FCSTD DOCUMENT  (FreeCAD 0.18R16110 (Git))
Label: plate
License: All rights reserved
LicenseURL: http://en.wikipedia.org/wiki/All_rights_reserved
objects: Part::Part2DObjectPython×463, App::DocumentObjectGroup×68
note: 463 computed .brp shape members not serialized (recipe doc carries the construction recipe); baked Part::Feature solids carry a one-line shape summary decoded from their .brp

FEATURE [Part::Part2DObjectPython] Arc  # Draft 2D object (typed FeaturePython)
  FirstAngle = 90
  LastAngle = 180
  MakeFace = true
  Placement = pos=(2.8,-2.8,0) rot=(0,0,1;0rad)
  Radius = 0.3
FEATURE [Part::Part2DObjectPython] Arc001  # Draft 2D object (typed FeaturePython)
  FirstAngle = 90
  LastAngle = 180
  MakeFace = true
  Placement = pos=(16.2,-2.8,0) rot=(0,0,-1;1.5708rad)
  Radius = 0.3
FEATURE [Part::Part2DObjectPython] Arc002  # Draft 2D object (typed FeaturePython)
  FirstAngle = 90
  LastAngle = 180
  MakeFace = true
  Placement = pos=(16.2,-16.2,0) rot=(0,0,1;3.14159rad)
  Radius = 0.3
FEATURE [Part::Part2DObjectPython] Arc003  # Draft 2D object (typed FeaturePython)
  FirstAngle = 90
  LastAngle = 180
  MakeFace = true
  Placement = pos=(2.8,-16.2,0) rot=(0,0,1;1.5708rad)
  Radius = 0.3
FEATURE [Part::Part2DObjectPython] Line012  # Draft 2D object (typed FeaturePython)
  ChamferSize = 0
  Closed = false
  End = (16.2,-2.5,0)
  FilletRadius = 0
  Length = 13.4
  MakeFace = true
  Points = (2) [(2.8,-2.5,0),(16.2,-2.5,0)]
  Start = (2.8,-2.5,0)
  Subdivisions = 0
FEATURE [Part::Part2DObjectPython] Line013  # Draft 2D object (typed FeaturePython)
  ChamferSize = 0
  Closed = false
  End = (16.5,-16.2,0)
  FilletRadius = 0
  Length = 13.4
  MakeFace = true
  Points = (2) [(16.5,-2.8,0),(16.5,-16.2,0)]
  Start = (16.5,-2.8,0)
  Subdivisions = 0
FEATURE [Part::Part2DObjectPython] Line014  # Draft 2D object (typed FeaturePython)
  ChamferSize = 0
  Closed = false
  End = (2.8,-16.5,0)
  FilletRadius = 0
  Length = 13.4
  MakeFace = true
  Points = (2) [(16.2,-16.5,0),(2.8,-16.5,0)]
  Start = (16.2,-16.5,0)
  Subdivisions = 0
FEATURE [Part::Part2DObjectPython] Line015  # Draft 2D object (typed FeaturePython)
  ChamferSize = 0
  Closed = false
  End = (2.5,-2.8,0)
  FilletRadius = 0
  Length = 13.4
  MakeFace = true
  Points = (2) [(2.5,-16.2,0),(2.5,-2.8,0)]
  Start = (2.5,-16.2,0)
  Subdivisions = 0
FEATURE [App::DocumentObjectGroup] Group
  Group = -> [Arc,Arc001,Arc002,Arc003,Line012,Line013,Line014,Line015]
FEATURE [Part::Part2DObjectPython] Arc004  # Draft 2D object (typed FeaturePython)
  FirstAngle = 90
  LastAngle = 180
  MakeFace = true
  Placement = pos=(21.8,-2.8,0) rot=(0,0,1;0rad)
  Radius = 0.3
FEATURE [Part::Part2DObjectPython] Line020  # Draft 2D object (typed FeaturePython)
  ChamferSize = 0
  Closed = false
  End = (21.8,-16.5,0)
  FilletRadius = 0
  Length = 13.4
  MakeFace = true
  Placement = pos=(19,0,0) rot=(0,0,1;0rad)
  Points = (2) [(16.2,-16.5,0),(2.8,-16.5,0)]
  Start = (35.2,-16.5,0)
  Subdivisions = 0
FEATURE [Part::Part2DObjectPython] Arc005  # Draft 2D object (typed FeaturePython)
  FirstAngle = 90
  LastAngle = 180
  MakeFace = true
  Placement = pos=(35.2,-16.2,0) rot=(0,0,1;3.14159rad)
  Radius = 0.3
FEATURE [Part::Part2DObjectPython] Line022  # Draft 2D object (typed FeaturePython)
  ChamferSize = 0
  Closed = false
  End = (21.5,-2.8,0)
  FilletRadius = 0
  Length = 13.4
  MakeFace = true
  Placement = pos=(19,0,0) rot=(0,0,1;0rad)
  Points = (2) [(2.5,-16.2,0),(2.5,-2.8,0)]
  Start = (21.5,-16.2,0)
  Subdivisions = 0
FEATURE [Part::Part2DObjectPython] Arc006  # Draft 2D object (typed FeaturePython)
  FirstAngle = 90
  LastAngle = 180
  MakeFace = true
  Placement = pos=(21.8,-16.2,0) rot=(0,0,1;1.5708rad)
  Radius = 0.3
FEATURE [Part::Part2DObjectPython] Line023  # Draft 2D object (typed FeaturePython)
  ChamferSize = 0
  Closed = false
  End = (35.2,-2.5,0)
  FilletRadius = 0
  Length = 13.4
  MakeFace = true
  Placement = pos=(19,0,0) rot=(0,0,1;0rad)
  Points = (2) [(2.8,-2.5,0),(16.2,-2.5,0)]
  Start = (21.8,-2.5,0)
  Subdivisions = 0
FEATURE [Part::Part2DObjectPython] Arc007  # Draft 2D object (typed FeaturePython)
  FirstAngle = 90
  LastAngle = 180
  MakeFace = true
  Placement = pos=(35.2,-2.8,0) rot=(0,0,-1;1.5708rad)
  Radius = 0.3
FEATURE [App::DocumentObjectGroup] Group001
  Group = -> [Arc004,Arc007,Arc005,Arc006,Line023,Line020,Line022]
FEATURE [Part::Part2DObjectPython] Arc008  # Draft 2D object (typed FeaturePython)
  FirstAngle = 90
  LastAngle = 180
  MakeFace = true
  Placement = pos=(40.8,-2.8,0) rot=(0,0,1;0rad)
  Radius = 0.3
FEATURE [Part::Part2DObjectPython] Line030  # Draft 2D object (typed FeaturePython)
  ChamferSize = 0
  Closed = false
  End = (40.8,-16.5,0)
  FilletRadius = 0
  Length = 13.4
  MakeFace = true
  Placement = pos=(38,0,0) rot=(0,0,1;0rad)
  Points = (2) [(16.2,-16.5,0),(2.8,-16.5,0)]
  Start = (54.2,-16.5,0)
  Subdivisions = 0
FEATURE [Part::Part2DObjectPython] Line031  # Draft 2D object (typed FeaturePython)
  ChamferSize = 0
  Closed = false
  End = (54.5,-16.2,0)
  FilletRadius = 0
  Length = 13.4
  MakeFace = true
  Placement = pos=(38,0,0) rot=(0,0,1;0rad)
  Points = (2) [(16.5,-2.8,0),(16.5,-16.2,0)]
  Start = (54.5,-2.8,0)
  Subdivisions = 0
FEATURE [Part::Part2DObjectPython] Arc009  # Draft 2D object (typed FeaturePython)
  FirstAngle = 90
  LastAngle = 180
  MakeFace = true
  Placement = pos=(54.2,-16.2,0) rot=(0,0,1;3.14159rad)
  Radius = 0.3
FEATURE [Part::Part2DObjectPython] Arc010  # Draft 2D object (typed FeaturePython)
  FirstAngle = 90
  LastAngle = 180
  MakeFace = true
  Placement = pos=(40.8,-16.2,0) rot=(0,0,1;1.5708rad)
  Radius = 0.3
FEATURE [Part::Part2DObjectPython] Line033  # Draft 2D object (typed FeaturePython)
  ChamferSize = 0
  Closed = false
  End = (54.2,-2.5,0)
  FilletRadius = 0
  Length = 13.4
  MakeFace = true
  Placement = pos=(38,0,0) rot=(0,0,1;0rad)
  Points = (2) [(2.8,-2.5,0),(16.2,-2.5,0)]
  Start = (40.8,-2.5,0)
  Subdivisions = 0
FEATURE [Part::Part2DObjectPython] Arc011  # Draft 2D object (typed FeaturePython)
  FirstAngle = 90
  LastAngle = 180
  MakeFace = true
  Placement = pos=(54.2,-2.8,0) rot=(0,0,-1;1.5708rad)
  Radius = 0.3
FEATURE [App::DocumentObjectGroup] Group002
  Group = -> [Arc008,Arc011,Arc009,Arc010,Line033,Line031,Line030]
FEATURE [Part::Part2DObjectPython] Arc012  # Draft 2D object (typed FeaturePython)
  FirstAngle = 90
  LastAngle = 180
  MakeFace = true
  Placement = pos=(59.8,-2.8,0) rot=(0,0,1;0rad)
  Radius = 0.3
FEATURE [Part::Part2DObjectPython] Line040  # Draft 2D object (typed FeaturePython)
  ChamferSize = 0
  Closed = false
  End = (59.8,-16.5,0)
  FilletRadius = 0
  Length = 13.4
  MakeFace = true
  Placement = pos=(57,0,0) rot=(0,0,1;0rad)
  Points = (2) [(16.2,-16.5,0),(2.8,-16.5,0)]
  Start = (73.2,-16.5,0)
  Subdivisions = 0
FEATURE [Part::Part2DObjectPython] Line041  # Draft 2D object (typed FeaturePython)
  ChamferSize = 0
  Closed = false
  End = (73.5,-16.2,0)
  FilletRadius = 0
  Length = 13.4
  MakeFace = true
  Placement = pos=(57,0,0) rot=(0,0,1;0rad)
  Points = (2) [(16.5,-2.8,0),(16.5,-16.2,0)]
  Start = (73.5,-2.8,0)
  Subdivisions = 0
FEATURE [Part::Part2DObjectPython] Arc013  # Draft 2D object (typed FeaturePython)
  FirstAngle = 90
  LastAngle = 180
  MakeFace = true
  Placement = pos=(73.2,-16.2,0) rot=(0,0,1;3.14159rad)
  Radius = 0.3
FEATURE [Part::Part2DObjectPython] Line042  # Draft 2D object (typed FeaturePython)
  ChamferSize = 0
  Closed = false
  End = (59.5,-2.8,0)
  FilletRadius = 0
  Length = 13.4
  MakeFace = true
  Placement = pos=(57,0,0) rot=(0,0,1;0rad)
  Points = (2) [(2.5,-16.2,0),(2.5,-2.8,0)]
  Start = (59.5,-16.2,0)
  Subdivisions = 0
FEATURE [Part::Part2DObjectPython] Arc014  # Draft 2D object (typed FeaturePython)
  FirstAngle = 90
  LastAngle = 180
  MakeFace = true
  Placement = pos=(59.8,-16.2,0) rot=(0,0,1;1.5708rad)
  Radius = 0.3
FEATURE [Part::Part2DObjectPython] Line043  # Draft 2D object (typed FeaturePython)
  ChamferSize = 0
  Closed = false
  End = (73.2,-2.5,0)
  FilletRadius = 0
  Length = 13.4
  MakeFace = true
  Placement = pos=(57,0,0) rot=(0,0,1;0rad)
  Points = (2) [(2.8,-2.5,0),(16.2,-2.5,0)]
  Start = (59.8,-2.5,0)
  Subdivisions = 0
FEATURE [Part::Part2DObjectPython] Arc015  # Draft 2D object (typed FeaturePython)
  FirstAngle = 90
  LastAngle = 180
  MakeFace = true
  Placement = pos=(73.2,-2.8,0) rot=(0,0,-1;1.5708rad)
  Radius = 0.3
FEATURE [App::DocumentObjectGroup] Group003
  Group = -> [Arc012,Arc015,Arc013,Arc014,Line043,Line041,Line040,Line042]
FEATURE [Part::Part2DObjectPython] Arc016  # Draft 2D object (typed FeaturePython)
  FirstAngle = 90
  LastAngle = 180
  MakeFace = true
  Placement = pos=(78.8,-2.8,0) rot=(0,0,1;0rad)
  Radius = 0.3
FEATURE [Part::Part2DObjectPython] Line050  # Draft 2D object (typed FeaturePython)
  ChamferSize = 0
  Closed = false
  End = (78.8,-16.5,0)
  FilletRadius = 0
  Length = 13.4
  MakeFace = true
  Placement = pos=(76,0,0) rot=(0,0,1;0rad)
  Points = (2) [(16.2,-16.5,0),(2.8,-16.5,0)]
  Start = (92.2,-16.5,0)
  Subdivisions = 0
FEATURE [Part::Part2DObjectPython] Line051  # Draft 2D object (typed FeaturePython)
  ChamferSize = 0
  Closed = false
  End = (92.5,-16.2,0)
  FilletRadius = 0
  Length = 13.4
  MakeFace = true
  Placement = pos=(76,0,0) rot=(0,0,1;0rad)
  Points = (2) [(16.5,-2.8,0),(16.5,-16.2,0)]
  Start = (92.5,-2.8,0)
  Subdivisions = 0
FEATURE [Part::Part2DObjectPython] Arc017  # Draft 2D object (typed FeaturePython)
  FirstAngle = 90
  LastAngle = 180
  MakeFace = true
  Placement = pos=(92.2,-16.2,0) rot=(0,0,1;3.14159rad)
  Radius = 0.3
FEATURE [Part::Part2DObjectPython] Line052  # Draft 2D object (typed FeaturePython)
  ChamferSize = 0
  Closed = false
  End = (78.5,-2.8,0)
  FilletRadius = 0
  Length = 13.4
  MakeFace = true
  Placement = pos=(76,0,0) rot=(0,0,1;0rad)
  Points = (2) [(2.5,-16.2,0),(2.5,-2.8,0)]
  Start = (78.5,-16.2,0)
  Subdivisions = 0
FEATURE [Part::Part2DObjectPython] Arc018  # Draft 2D object (typed FeaturePython)
  FirstAngle = 90
  LastAngle = 180
  MakeFace = true
  Placement = pos=(78.8,-16.2,0) rot=(0,0,1;1.5708rad)
  Radius = 0.3
FEATURE [Part::Part2DObjectPython] Line053  # Draft 2D object (typed FeaturePython)
  ChamferSize = 0
  Closed = false
  End = (92.2,-2.5,0)
  FilletRadius = 0
  Length = 13.4
  MakeFace = true
  Placement = pos=(76,0,0) rot=(0,0,1;0rad)
  Points = (2) [(2.8,-2.5,0),(16.2,-2.5,0)]
  Start = (78.8,-2.5,0)
  Subdivisions = 0
FEATURE [Part::Part2DObjectPython] Arc019  # Draft 2D object (typed FeaturePython)
  FirstAngle = 90
  LastAngle = 180
  MakeFace = true
  Placement = pos=(92.2,-2.8,0) rot=(0,0,-1;1.5708rad)
  Radius = 0.3
FEATURE [App::DocumentObjectGroup] Group004
  Group = -> [Arc016,Arc019,Arc017,Arc018,Line053,Line051,Line050,Line052]
FEATURE [Part::Part2DObjectPython] Arc020  # Draft 2D object (typed FeaturePython)
  FirstAngle = 90
  LastAngle = 180
  MakeFace = true
  Placement = pos=(97.8,-2.8,0) rot=(0,0,1;0rad)
  Radius = 0.3
FEATURE [Part::Part2DObjectPython] Line060  # Draft 2D object (typed FeaturePython)
  ChamferSize = 0
  Closed = false
  End = (97.8,-16.5,0)
  FilletRadius = 0
  Length = 13.4
  MakeFace = true
  Placement = pos=(95,0,0) rot=(0,0,1;0rad)
  Points = (2) [(16.2,-16.5,0),(2.8,-16.5,0)]
  Start = (111.2,-16.5,0)
  Subdivisions = 0
FEATURE [Part::Part2DObjectPython] Arc021  # Draft 2D object (typed FeaturePython)
  FirstAngle = 90
  LastAngle = 180
  MakeFace = true
  Placement = pos=(111.2,-16.2,0) rot=(0,0,1;3.14159rad)
  Radius = 0.3
FEATURE [Part::Part2DObjectPython] Line062  # Draft 2D object (typed FeaturePython)
  ChamferSize = 0
  Closed = false
  End = (97.5,-2.8,0)
  FilletRadius = 0
  Length = 13.4
  MakeFace = true
  Placement = pos=(95,0,0) rot=(0,0,1;0rad)
  Points = (2) [(2.5,-16.2,0),(2.5,-2.8,0)]
  Start = (97.5,-16.2,0)
  Subdivisions = 0
FEATURE [Part::Part2DObjectPython] Arc022  # Draft 2D object (typed FeaturePython)
  FirstAngle = 90
  LastAngle = 180
  MakeFace = true
  Placement = pos=(97.8,-16.2,0) rot=(0,0,1;1.5708rad)
  Radius = 0.3
FEATURE [Part::Part2DObjectPython] Line063  # Draft 2D object (typed FeaturePython)
  ChamferSize = 0
  Closed = false
  End = (111.2,-2.5,0)
  FilletRadius = 0
  Length = 13.4
  MakeFace = true
  Placement = pos=(95,0,0) rot=(0,0,1;0rad)
  Points = (2) [(2.8,-2.5,0),(16.2,-2.5,0)]
  Start = (97.8,-2.5,0)
  Subdivisions = 0
FEATURE [Part::Part2DObjectPython] Arc023  # Draft 2D object (typed FeaturePython)
  FirstAngle = 90
  LastAngle = 180
  MakeFace = true
  Placement = pos=(111.2,-2.8,0) rot=(0,0,-1;1.5708rad)
  Radius = 0.3
FEATURE [App::DocumentObjectGroup] Group005
  Group = -> [Arc020,Arc023,Arc021,Arc022,Line063,Line060,Line062]
FEATURE [Part::Part2DObjectPython] Arc024  # Draft 2D object (typed FeaturePython)
  FirstAngle = 90
  LastAngle = 180
  MakeFace = true
  Placement = pos=(116.8,-2.8,0) rot=(0,0,1;0rad)
  Radius = 0.3
FEATURE [Part::Part2DObjectPython] Line070  # Draft 2D object (typed FeaturePython)
  ChamferSize = 0
  Closed = false
  End = (116.8,-16.5,0)
  FilletRadius = 0
  Length = 13.4
  MakeFace = true
  Placement = pos=(114,0,0) rot=(0,0,1;0rad)
  Points = (2) [(16.2,-16.5,0),(2.8,-16.5,0)]
  Start = (130.2,-16.5,0)
  Subdivisions = 0
FEATURE [Part::Part2DObjectPython] Line071  # Draft 2D object (typed FeaturePython)
  ChamferSize = 0
  Closed = false
  End = (130.5,-16.2,0)
  FilletRadius = 0
  Length = 13.4
  MakeFace = true
  Placement = pos=(114,0,0) rot=(0,0,1;0rad)
  Points = (2) [(16.5,-2.8,0),(16.5,-16.2,0)]
  Start = (130.5,-2.8,0)
  Subdivisions = 0
FEATURE [Part::Part2DObjectPython] Arc025  # Draft 2D object (typed FeaturePython)
  FirstAngle = 90
  LastAngle = 180
  MakeFace = true
  Placement = pos=(130.2,-16.2,0) rot=(0,0,1;3.14159rad)
  Radius = 0.3
FEATURE [Part::Part2DObjectPython] Arc026  # Draft 2D object (typed FeaturePython)
  FirstAngle = 90
  LastAngle = 180
  MakeFace = true
  Placement = pos=(116.8,-16.2,0) rot=(0,0,1;1.5708rad)
  Radius = 0.3
FEATURE [Part::Part2DObjectPython] Line073  # Draft 2D object (typed FeaturePython)
  ChamferSize = 0
  Closed = false
  End = (130.2,-2.5,0)
  FilletRadius = 0
  Length = 13.4
  MakeFace = true
  Placement = pos=(114,0,0) rot=(0,0,1;0rad)
  Points = (2) [(2.8,-2.5,0),(16.2,-2.5,0)]
  Start = (116.8,-2.5,0)
  Subdivisions = 0
FEATURE [Part::Part2DObjectPython] Arc027  # Draft 2D object (typed FeaturePython)
  FirstAngle = 90
  LastAngle = 180
  MakeFace = true
  Placement = pos=(130.2,-2.8,0) rot=(0,0,-1;1.5708rad)
  Radius = 0.3
FEATURE [App::DocumentObjectGroup] Group006
  Group = -> [Arc024,Arc027,Arc025,Arc026,Line073,Line071,Line070]
FEATURE [Part::Part2DObjectPython] Arc028  # Draft 2D object (typed FeaturePython)
  FirstAngle = 90
  LastAngle = 180
  MakeFace = true
  Placement = pos=(135.8,-2.8,0) rot=(0,0,1;0rad)
  Radius = 0.3
FEATURE [Part::Part2DObjectPython] Line080  # Draft 2D object (typed FeaturePython)
  ChamferSize = 0
  Closed = false
  End = (135.8,-16.5,0)
  FilletRadius = 0
  Length = 13.4
  MakeFace = true
  Placement = pos=(133,0,0) rot=(0,0,1;0rad)
  Points = (2) [(16.2,-16.5,0),(2.8,-16.5,0)]
  Start = (149.2,-16.5,0)
  Subdivisions = 0
FEATURE [Part::Part2DObjectPython] Line081  # Draft 2D object (typed FeaturePython)
  ChamferSize = 0
  Closed = false
  End = (149.5,-16.2,0)
  FilletRadius = 0
  Length = 13.4
  MakeFace = true
  Placement = pos=(133,0,0) rot=(0,0,1;0rad)
  Points = (2) [(16.5,-2.8,0),(16.5,-16.2,0)]
  Start = (149.5,-2.8,0)
  Subdivisions = 0
FEATURE [Part::Part2DObjectPython] Arc029  # Draft 2D object (typed FeaturePython)
  FirstAngle = 90
  LastAngle = 180
  MakeFace = true
  Placement = pos=(149.2,-16.2,0) rot=(0,0,1;3.14159rad)
  Radius = 0.3
FEATURE [Part::Part2DObjectPython] Line082  # Draft 2D object (typed FeaturePython)
  ChamferSize = 0
  Closed = false
  End = (135.5,-2.8,0)
  FilletRadius = 0
  Length = 13.4
  MakeFace = true
  Placement = pos=(133,0,0) rot=(0,0,1;0rad)
  Points = (2) [(2.5,-16.2,0),(2.5,-2.8,0)]
  Start = (135.5,-16.2,0)
  Subdivisions = 0
FEATURE [Part::Part2DObjectPython] Arc030  # Draft 2D object (typed FeaturePython)
  FirstAngle = 90
  LastAngle = 180
  MakeFace = true
  Placement = pos=(135.8,-16.2,0) rot=(0,0,1;1.5708rad)
  Radius = 0.3
FEATURE [Part::Part2DObjectPython] Line083  # Draft 2D object (typed FeaturePython)
  ChamferSize = 0
  Closed = false
  End = (149.2,-2.5,0)
  FilletRadius = 0
  Length = 13.4
  MakeFace = true
  Placement = pos=(133,0,0) rot=(0,0,1;0rad)
  Points = (2) [(2.8,-2.5,0),(16.2,-2.5,0)]
  Start = (135.8,-2.5,0)
  Subdivisions = 0
FEATURE [Part::Part2DObjectPython] Arc031  # Draft 2D object (typed FeaturePython)
  FirstAngle = 90
  LastAngle = 180
  MakeFace = true
  Placement = pos=(149.2,-2.8,0) rot=(0,0,-1;1.5708rad)
  Radius = 0.3
FEATURE [App::DocumentObjectGroup] Group007
  Group = -> [Arc028,Arc031,Arc029,Arc030,Line083,Line081,Line080,Line082]
FEATURE [Part::Part2DObjectPython] Arc036  # Draft 2D object (typed FeaturePython)
  FirstAngle = 90
  LastAngle = 180
  MakeFace = true
  Placement = pos=(154.8,-2.8,0) rot=(0,0,1;0rad)
  Radius = 0.3
FEATURE [Part::Part2DObjectPython] Line100  # Draft 2D object (typed FeaturePython)
  ChamferSize = 0
  Closed = false
  End = (154.8,-16.5,0)
  FilletRadius = 0
  Length = 13.4
  MakeFace = true
  Placement = pos=(152,0,0) rot=(0,0,1;0rad)
  Points = (2) [(16.2,-16.5,0),(2.8,-16.5,0)]
  Start = (168.2,-16.5,0)
  Subdivisions = 0
FEATURE [Part::Part2DObjectPython] Line101  # Draft 2D object (typed FeaturePython)
  ChamferSize = 0
  Closed = false
  End = (168.5,-16.2,0)
  FilletRadius = 0
  Length = 13.4
  MakeFace = true
  Placement = pos=(152,0,0) rot=(0,0,1;0rad)
  Points = (2) [(16.5,-2.8,0),(16.5,-16.2,0)]
  Start = (168.5,-2.8,0)
  Subdivisions = 0
FEATURE [Part::Part2DObjectPython] Arc037  # Draft 2D object (typed FeaturePython)
  FirstAngle = 90
  LastAngle = 180
  MakeFace = true
  Placement = pos=(168.2,-16.2,0) rot=(0,0,1;3.14159rad)
  Radius = 0.3
FEATURE [Part::Part2DObjectPython] Line102  # Draft 2D object (typed FeaturePython)
  ChamferSize = 0
  Closed = false
  End = (154.5,-2.8,0)
  FilletRadius = 0
  Length = 13.4
  MakeFace = true
  Placement = pos=(152,0,0) rot=(0,0,1;0rad)
  Points = (2) [(2.5,-16.2,0),(2.5,-2.8,0)]
  Start = (154.5,-16.2,0)
  Subdivisions = 0
FEATURE [Part::Part2DObjectPython] Arc038  # Draft 2D object (typed FeaturePython)
  FirstAngle = 90
  LastAngle = 180
  MakeFace = true
  Placement = pos=(154.8,-16.2,0) rot=(0,0,1;1.5708rad)
  Radius = 0.3
FEATURE [Part::Part2DObjectPython] Line103  # Draft 2D object (typed FeaturePython)
  ChamferSize = 0
  Closed = false
  End = (168.2,-2.5,0)
  FilletRadius = 0
  Length = 13.4
  MakeFace = true
  Placement = pos=(152,0,0) rot=(0,0,1;0rad)
  Points = (2) [(2.8,-2.5,0),(16.2,-2.5,0)]
  Start = (154.8,-2.5,0)
  Subdivisions = 0
FEATURE [Part::Part2DObjectPython] Arc039  # Draft 2D object (typed FeaturePython)
  FirstAngle = 90
  LastAngle = 180
  MakeFace = true
  Placement = pos=(168.2,-2.8,0) rot=(0,0,-1;1.5708rad)
  Radius = 0.3
FEATURE [App::DocumentObjectGroup] Group009
  Group = -> [Arc036,Arc039,Arc037,Arc038,Line103,Line101,Line100,Line102]
FEATURE [Part::Part2DObjectPython] Arc040  # Draft 2D object (typed FeaturePython)
  FirstAngle = 90
  LastAngle = 180
  MakeFace = true
  Placement = pos=(173.8,-2.8,0) rot=(0,0,1;0rad)
  Radius = 0.3
FEATURE [Part::Part2DObjectPython] Line110  # Draft 2D object (typed FeaturePython)
  ChamferSize = 0
  Closed = false
  End = (173.8,-16.5,0)
  FilletRadius = 0
  Length = 13.4
  MakeFace = true
  Placement = pos=(171,0,0) rot=(0,0,1;0rad)
  Points = (2) [(16.2,-16.5,0),(2.8,-16.5,0)]
  Start = (187.2,-16.5,0)
  Subdivisions = 0
FEATURE [Part::Part2DObjectPython] Line111  # Draft 2D object (typed FeaturePython)
  ChamferSize = 0
  Closed = false
  End = (187.5,-16.2,0)
  FilletRadius = 0
  Length = 13.4
  MakeFace = true
  Placement = pos=(171,0,0) rot=(0,0,1;0rad)
  Points = (2) [(16.5,-2.8,0),(16.5,-16.2,0)]
  Start = (187.5,-2.8,0)
  Subdivisions = 0
FEATURE [Part::Part2DObjectPython] Arc041  # Draft 2D object (typed FeaturePython)
  FirstAngle = 90
  LastAngle = 180
  MakeFace = true
  Placement = pos=(187.2,-16.2,0) rot=(0,0,1;3.14159rad)
  Radius = 0.3
FEATURE [Part::Part2DObjectPython] Line112  # Draft 2D object (typed FeaturePython)
  ChamferSize = 0
  Closed = false
  End = (173.5,-2.8,0)
  FilletRadius = 0
  Length = 13.4
  MakeFace = true
  Placement = pos=(171,0,0) rot=(0,0,1;0rad)
  Points = (2) [(2.5,-16.2,0),(2.5,-2.8,0)]
  Start = (173.5,-16.2,0)
  Subdivisions = 0
FEATURE [Part::Part2DObjectPython] Arc042  # Draft 2D object (typed FeaturePython)
  FirstAngle = 90
  LastAngle = 180
  MakeFace = true
  Placement = pos=(173.8,-16.2,0) rot=(0,0,1;1.5708rad)
  Radius = 0.3
FEATURE [Part::Part2DObjectPython] Line113  # Draft 2D object (typed FeaturePython)
  ChamferSize = 0
  Closed = false
  End = (187.2,-2.5,0)
  FilletRadius = 0
  Length = 13.4
  MakeFace = true
  Placement = pos=(171,0,0) rot=(0,0,1;0rad)
  Points = (2) [(2.8,-2.5,0),(16.2,-2.5,0)]
  Start = (173.8,-2.5,0)
  Subdivisions = 0
FEATURE [Part::Part2DObjectPython] Arc043  # Draft 2D object (typed FeaturePython)
  FirstAngle = 90
  LastAngle = 180
  MakeFace = true
  Placement = pos=(187.2,-2.8,0) rot=(0,0,-1;1.5708rad)
  Radius = 0.3
FEATURE [App::DocumentObjectGroup] Group010
  Group = -> [Arc040,Arc043,Arc041,Arc042,Line113,Line111,Line110,Line112]
FEATURE [Part::Part2DObjectPython] Arc044  # Draft 2D object (typed FeaturePython)
  FirstAngle = 90
  LastAngle = 180
  MakeFace = true
  Placement = pos=(192.8,-2.8,0) rot=(0,0,1;0rad)
  Radius = 0.3
FEATURE [Part::Part2DObjectPython] Line120  # Draft 2D object (typed FeaturePython)
  ChamferSize = 0
  Closed = false
  End = (192.8,-16.5,0)
  FilletRadius = 0
  Length = 13.4
  MakeFace = true
  Placement = pos=(190,0,0) rot=(0,0,1;0rad)
  Points = (2) [(16.2,-16.5,0),(2.8,-16.5,0)]
  Start = (206.2,-16.5,0)
  Subdivisions = 0
FEATURE [Part::Part2DObjectPython] Arc045  # Draft 2D object (typed FeaturePython)
  FirstAngle = 90
  LastAngle = 180
  MakeFace = true
  Placement = pos=(206.2,-16.2,0) rot=(0,0,1;3.14159rad)
  Radius = 0.3
FEATURE [Part::Part2DObjectPython] Line122  # Draft 2D object (typed FeaturePython)
  ChamferSize = 0
  Closed = false
  End = (192.5,-2.8,0)
  FilletRadius = 0
  Length = 13.4
  MakeFace = true
  Placement = pos=(190,0,0) rot=(0,0,1;0rad)
  Points = (2) [(2.5,-16.2,0),(2.5,-2.8,0)]
  Start = (192.5,-16.2,0)
  Subdivisions = 0
FEATURE [Part::Part2DObjectPython] Arc046  # Draft 2D object (typed FeaturePython)
  FirstAngle = 90
  LastAngle = 180
  MakeFace = true
  Placement = pos=(192.8,-16.2,0) rot=(0,0,1;1.5708rad)
  Radius = 0.3
FEATURE [Part::Part2DObjectPython] Line123  # Draft 2D object (typed FeaturePython)
  ChamferSize = 0
  Closed = false
  End = (206.2,-2.5,0)
  FilletRadius = 0
  Length = 13.4
  MakeFace = true
  Placement = pos=(190,0,0) rot=(0,0,1;0rad)
  Points = (2) [(2.8,-2.5,0),(16.2,-2.5,0)]
  Start = (192.8,-2.5,0)
  Subdivisions = 0
FEATURE [Part::Part2DObjectPython] Arc047  # Draft 2D object (typed FeaturePython)
  FirstAngle = 90
  LastAngle = 180
  MakeFace = true
  Placement = pos=(206.2,-2.8,0) rot=(0,0,-1;1.5708rad)
  Radius = 0.3
FEATURE [App::DocumentObjectGroup] Group011
  Group = -> [Arc044,Arc047,Arc045,Arc046,Line123,Line120,Line122]
FEATURE [Part::Part2DObjectPython] Arc048  # Draft 2D object (typed FeaturePython)
  FirstAngle = 90
  LastAngle = 180
  MakeFace = true
  Placement = pos=(211.8,-2.8,0) rot=(0,0,1;0rad)
  Radius = 0.3
FEATURE [Part::Part2DObjectPython] Arc050  # Draft 2D object (typed FeaturePython)
  FirstAngle = 90
  LastAngle = 180
  MakeFace = true
  Placement = pos=(211.8,-16.2,0) rot=(0,0,1;1.5708rad)
  Radius = 0.3
FEATURE [Part::Part2DObjectPython] Line136  # Draft 2D object (typed FeaturePython)
  ChamferSize = 0
  Closed = false
  End = (244.5,-16.2,0)
  FilletRadius = 0
  Length = 13.4
  MakeFace = true
  Placement = pos=(228,0,0) rot=(0,0,1;0rad)
  Points = (2) [(16.5,-2.8,0),(16.5,-16.2,0)]
  Start = (244.5,-2.8,0)
  Subdivisions = 0
FEATURE [Part::Part2DObjectPython] Arc054  # Draft 2D object (typed FeaturePython)
  FirstAngle = 90
  LastAngle = 180
  MakeFace = true
  Placement = pos=(244.2,-16.2,0) rot=(0,0,1;3.14159rad)
  Radius = 0.3
FEATURE [Part::Part2DObjectPython] Arc055  # Draft 2D object (typed FeaturePython)
  FirstAngle = 90
  LastAngle = 180
  MakeFace = true
  Placement = pos=(244.2,-2.8,0) rot=(0,0,-1;1.5708rad)
  Radius = 0.3
FEATURE [Part::Part2DObjectPython] Arc212  # Draft 2D object (typed FeaturePython)
  FirstAngle = 90
  LastAngle = 180
  MakeFace = true
  Placement = pos=(2.5,-2.5,0) rot=(0,0,1;0rad)
  Radius = 2
FEATURE [Part::Part2DObjectPython] Arc213  # Draft 2D object (typed FeaturePython)
  FirstAngle = 90
  LastAngle = 180
  MakeFace = true
  Placement = pos=(244.5,-73.5,0) rot=(0,0,1;3.14159rad)
  Radius = 2
FEATURE [Part::Part2DObjectPython] Arc214  # Draft 2D object (typed FeaturePython)
  FirstAngle = 90
  LastAngle = 180
  MakeFace = true
  Placement = pos=(244.5,-2.5,0) rot=(0,0,-1;1.5708rad)
  Radius = 2
FEATURE [Part::Part2DObjectPython] Arc215  # Draft 2D object (typed FeaturePython)
  FirstAngle = 90
  LastAngle = 180
  MakeFace = true
  Placement = pos=(2.5,-73.5,0) rot=(0,0,1;1.5708rad)
  Radius = 2
FEATURE [Part::Part2DObjectPython] Arc216  # Draft 2D object (typed FeaturePython)
  FirstAngle = 90
  LastAngle = 180
  MakeFace = true
  Placement = pos=(5.175,-21.8,0) rot=(0,0,1;0rad)
  Radius = 0.3
FEATURE [Part::Part2DObjectPython] Line412  # Draft 2D object (typed FeaturePython)
  ChamferSize = 0
  Closed = false
  End = (5.175,-35.5,0)
  FilletRadius = 0
  Length = 13.4
  MakeFace = true
  Placement = pos=(2.375,-19,0) rot=(0,0,1;0rad)
  Points = (2) [(16.2,-16.5,0),(2.8,-16.5,0)]
  Start = (18.575,-35.5,0)
  Subdivisions = 0
FEATURE [Part::Part2DObjectPython] Line413  # Draft 2D object (typed FeaturePython)
  ChamferSize = 0
  Closed = false
  End = (18.875,-35.2,0)
  FilletRadius = 0
  Length = 13.4
  MakeFace = true
  Placement = pos=(2.375,-19,0) rot=(0,0,1;0rad)
  Points = (2) [(16.5,-2.8,0),(16.5,-16.2,0)]
  Start = (18.875,-21.8,0)
  Subdivisions = 0
FEATURE [Part::Part2DObjectPython] Arc217  # Draft 2D object (typed FeaturePython)
  FirstAngle = 90
  LastAngle = 180
  MakeFace = true
  Placement = pos=(18.575,-35.2,0) rot=(0,0,1;3.14159rad)
  Radius = 0.3
FEATURE [Part::Part2DObjectPython] Line414  # Draft 2D object (typed FeaturePython)
  ChamferSize = 0
  Closed = false
  End = (4.875,-21.8,0)
  FilletRadius = 0
  Length = 13.4
  MakeFace = true
  Placement = pos=(2.375,-19,0) rot=(0,0,1;0rad)
  Points = (2) [(2.5,-16.2,0),(2.5,-2.8,0)]
  Start = (4.875,-35.2,0)
  Subdivisions = 0
FEATURE [Part::Part2DObjectPython] Arc218  # Draft 2D object (typed FeaturePython)
  FirstAngle = 90
  LastAngle = 180
  MakeFace = true
  Placement = pos=(5.175,-35.2,0) rot=(0,0,1;1.5708rad)
  Radius = 0.3
FEATURE [Part::Part2DObjectPython] Line415  # Draft 2D object (typed FeaturePython)
  ChamferSize = 0
  Closed = false
  End = (18.575,-21.5,0)
  FilletRadius = 0
  Length = 13.4
  MakeFace = true
  Placement = pos=(2.375,-19,0) rot=(0,0,1;0rad)
  Points = (2) [(2.8,-2.5,0),(16.2,-2.5,0)]
  Start = (5.175,-21.5,0)
  Subdivisions = 0
FEATURE [Part::Part2DObjectPython] Arc219  # Draft 2D object (typed FeaturePython)
  FirstAngle = 90
  LastAngle = 180
  MakeFace = true
  Placement = pos=(18.575,-21.8,0) rot=(0,0,-1;1.5708rad)
  Radius = 0.3
FEATURE [App::DocumentObjectGroup] Group016
  Group = -> [Arc216,Arc219,Arc217,Arc218,Line415,Line413,Line412,Line414]
FEATURE [Part::Part2DObjectPython] Arc220  # Draft 2D object (typed FeaturePython)
  FirstAngle = 90
  LastAngle = 180
  MakeFace = true
  Placement = pos=(77.95,-21.8,0) rot=(0,0,-1;1.5708rad)
  Radius = 0.3
FEATURE [Part::Part2DObjectPython] Line418  # Draft 2D object (typed FeaturePython)
  ChamferSize = 0
  Closed = false
  End = (59.25,-35.2,0)
  FilletRadius = 0
  Length = 13.4
  MakeFace = true
  Placement = pos=(42.75,-19,0) rot=(0,0,1;0rad)
  Points = (2) [(16.5,-2.8,0),(16.5,-16.2,0)]
  Start = (59.25,-21.8,0)
  Subdivisions = 0
FEATURE [Part::Part2DObjectPython] Line422  # Draft 2D object (typed FeaturePython)
  ChamferSize = 0
  Closed = false
  End = (45.25,-21.8,0)
  FilletRadius = 0
  Length = 13.4
  MakeFace = true
  Placement = pos=(42.75,-19,0) rot=(0,0,1;0rad)
  Points = (2) [(2.5,-16.2,0),(2.5,-2.8,0)]
  Start = (45.25,-35.2,0)
  Subdivisions = 0
FEATURE [Part::Part2DObjectPython] Arc221  # Draft 2D object (typed FeaturePython)
  FirstAngle = 90
  LastAngle = 180
  MakeFace = true
  Placement = pos=(58.95,-35.2,0) rot=(0,0,1;3.14159rad)
  Radius = 0.3
FEATURE [Part::Part2DObjectPython] Arc222  # Draft 2D object (typed FeaturePython)
  FirstAngle = 90
  LastAngle = 180
  MakeFace = true
  Placement = pos=(45.55,-35.2,0) rot=(0,0,1;1.5708rad)
  Radius = 0.3
FEATURE [Part::Part2DObjectPython] Arc223  # Draft 2D object (typed FeaturePython)
  FirstAngle = 90
  LastAngle = 180
  MakeFace = true
  Placement = pos=(64.55,-21.8,0) rot=(0,0,1;0rad)
  Radius = 0.3
FEATURE [Part::Part2DObjectPython] Line424  # Draft 2D object (typed FeaturePython)
  ChamferSize = 0
  Closed = false
  End = (58.95,-21.5,0)
  FilletRadius = 0
  Length = 13.4
  MakeFace = true
  Placement = pos=(42.75,-19,0) rot=(0,0,1;0rad)
  Points = (2) [(2.8,-2.5,0),(16.2,-2.5,0)]
  Start = (45.55,-21.5,0)
  Subdivisions = 0
FEATURE [Part::Part2DObjectPython] Arc224  # Draft 2D object (typed FeaturePython)
  FirstAngle = 90
  LastAngle = 180
  MakeFace = true
  Placement = pos=(83.55,-35.2,0) rot=(0,0,1;1.5708rad)
  Radius = 0.3
FEATURE [Part::Part2DObjectPython] Arc225  # Draft 2D object (typed FeaturePython)
  FirstAngle = 90
  LastAngle = 180
  MakeFace = true
  Placement = pos=(58.95,-21.8,0) rot=(0,0,-1;1.5708rad)
  Radius = 0.3
FEATURE [Part::Part2DObjectPython] Line426  # Draft 2D object (typed FeaturePython)
  ChamferSize = 0
  Closed = false
  End = (78.25,-35.2,0)
  FilletRadius = 0
  Length = 13.4
  MakeFace = true
  Placement = pos=(61.75,-19,0) rot=(0,0,1;0rad)
  Points = (2) [(16.5,-2.8,0),(16.5,-16.2,0)]
  Start = (78.25,-21.8,0)
  Subdivisions = 0
FEATURE [Part::Part2DObjectPython] Line427  # Draft 2D object (typed FeaturePython)
  ChamferSize = 0
  Closed = false
  End = (64.25,-21.8,0)
  FilletRadius = 0
  Length = 13.4
  MakeFace = true
  Placement = pos=(61.75,-19,0) rot=(0,0,1;0rad)
  Points = (2) [(2.5,-16.2,0),(2.5,-2.8,0)]
  Start = (64.25,-35.2,0)
  Subdivisions = 0
FEATURE [Part::Part2DObjectPython] Arc226  # Draft 2D object (typed FeaturePython)
  FirstAngle = 90
  LastAngle = 180
  MakeFace = true
  Placement = pos=(64.55,-35.2,0) rot=(0,0,1;1.5708rad)
  Radius = 0.3
FEATURE [Part::Part2DObjectPython] Line428  # Draft 2D object (typed FeaturePython)
  ChamferSize = 0
  Closed = false
  End = (77.95,-21.5,0)
  FilletRadius = 0
  Length = 13.4
  MakeFace = true
  Placement = pos=(61.75,-19,0) rot=(0,0,1;0rad)
  Points = (2) [(2.8,-2.5,0),(16.2,-2.5,0)]
  Start = (64.55,-21.5,0)
  Subdivisions = 0
FEATURE [Part::Part2DObjectPython] Arc227  # Draft 2D object (typed FeaturePython)
  FirstAngle = 90
  LastAngle = 180
  MakeFace = true
  Placement = pos=(77.95,-35.2,0) rot=(0,0,1;3.14159rad)
  Radius = 0.3
FEATURE [Part::Part2DObjectPython] Line429  # Draft 2D object (typed FeaturePython)
  ChamferSize = 0
  Closed = false
  End = (64.55,-35.5,0)
  FilletRadius = 0
  Length = 13.4
  MakeFace = true
  Placement = pos=(61.75,-19,0) rot=(0,0,1;0rad)
  Points = (2) [(16.2,-16.5,0),(2.8,-16.5,0)]
  Start = (77.95,-35.5,0)
  Subdivisions = 0
FEATURE [Part::Part2DObjectPython] Line430  # Draft 2D object (typed FeaturePython)
  ChamferSize = 0
  Closed = false
  End = (210.95,-21.5,0)
  FilletRadius = 0
  Length = 13.4
  MakeFace = true
  Placement = pos=(194.75,-19,0) rot=(0,0,1;0rad)
  Points = (2) [(2.8,-2.5,0),(16.2,-2.5,0)]
  Start = (197.55,-21.5,0)
  Subdivisions = 0
FEATURE [Part::Part2DObjectPython] Arc228  # Draft 2D object (typed FeaturePython)
  FirstAngle = 90
  LastAngle = 180
  MakeFace = true
  Placement = pos=(26.55,-21.8,0) rot=(0,0,1;0rad)
  Radius = 0.3
FEATURE [Part::Part2DObjectPython] Arc229  # Draft 2D object (typed FeaturePython)
  FirstAngle = 90
  LastAngle = 180
  MakeFace = true
  Placement = pos=(197.55,-35.2,0) rot=(0,0,1;1.5708rad)
  Radius = 0.3
FEATURE [Part::Part2DObjectPython] Line439  # Draft 2D object (typed FeaturePython)
  ChamferSize = 0
  Closed = false
  End = (83.55,-35.5,0)
  FilletRadius = 0
  Length = 13.4
  MakeFace = true
  Placement = pos=(80.75,-19,0) rot=(0,0,1;0rad)
  Points = (2) [(16.2,-16.5,0),(2.8,-16.5,0)]
  Start = (96.95,-35.5,0)
  Subdivisions = 0
FEATURE [Part::Part2DObjectPython] Line440  # Draft 2D object (typed FeaturePython)
  ChamferSize = 0
  Closed = false
  End = (97.25,-35.2,0)
  FilletRadius = 0
  Length = 13.4
  MakeFace = true
  Placement = pos=(80.75,-19,0) rot=(0,0,1;0rad)
  Points = (2) [(16.5,-2.8,0),(16.5,-16.2,0)]
  Start = (97.25,-21.8,0)
  Subdivisions = 0
FEATURE [Part::Part2DObjectPython] Arc230  # Draft 2D object (typed FeaturePython)
  FirstAngle = 90
  LastAngle = 180
  MakeFace = true
  Placement = pos=(83.55,-21.8,0) rot=(0,0,1;0rad)
  Radius = 0.3
FEATURE [Part::Part2DObjectPython] Line442  # Draft 2D object (typed FeaturePython)
  ChamferSize = 0
  Closed = false
  End = (45.55,-35.5,0)
  FilletRadius = 0
  Length = 13.4
  MakeFace = true
  Placement = pos=(42.75,-19,0) rot=(0,0,1;0rad)
  Points = (2) [(16.2,-16.5,0),(2.8,-16.5,0)]
  Start = (58.95,-35.5,0)
  Subdivisions = 0
FEATURE [Part::Part2DObjectPython] Line443  # Draft 2D object (typed FeaturePython)
  ChamferSize = 0
  Closed = false
  End = (26.55,-35.5,0)
  FilletRadius = 0
  Length = 13.4
  MakeFace = true
  Placement = pos=(23.75,-19,0) rot=(0,0,1;0rad)
  Points = (2) [(16.2,-16.5,0),(2.8,-16.5,0)]
  Start = (39.95,-35.5,0)
  Subdivisions = 0
FEATURE [Part::Part2DObjectPython] Line444  # Draft 2D object (typed FeaturePython)
  ChamferSize = 0
  Closed = false
  End = (40.25,-35.2,0)
  FilletRadius = 0
  Length = 13.4
  MakeFace = true
  Placement = pos=(23.75,-19,0) rot=(0,0,1;0rad)
  Points = (2) [(16.5,-2.8,0),(16.5,-16.2,0)]
  Start = (40.25,-21.8,0)
  Subdivisions = 0
FEATURE [Part::Part2DObjectPython] Line445  # Draft 2D object (typed FeaturePython)
  ChamferSize = 0
  Closed = false
  End = (83.25,-21.8,0)
  FilletRadius = 0
  Length = 13.4
  MakeFace = true
  Placement = pos=(80.75,-19,0) rot=(0,0,1;0rad)
  Points = (2) [(2.5,-16.2,0),(2.5,-2.8,0)]
  Start = (83.25,-35.2,0)
  Subdivisions = 0
FEATURE [Part::Part2DObjectPython] Arc231  # Draft 2D object (typed FeaturePython)
  FirstAngle = 90
  LastAngle = 180
  MakeFace = true
  Placement = pos=(39.95,-35.2,0) rot=(0,0,1;3.14159rad)
  Radius = 0.3
FEATURE [Part::Part2DObjectPython] Line446  # Draft 2D object (typed FeaturePython)
  ChamferSize = 0
  Closed = false
  End = (26.25,-21.8,0)
  FilletRadius = 0
  Length = 13.4
  MakeFace = true
  Placement = pos=(23.75,-19,0) rot=(0,0,1;0rad)
  Points = (2) [(2.5,-16.2,0),(2.5,-2.8,0)]
  Start = (26.25,-35.2,0)
  Subdivisions = 0
FEATURE [Part::Part2DObjectPython] Arc232  # Draft 2D object (typed FeaturePython)
  FirstAngle = 90
  LastAngle = 180
  MakeFace = true
  Placement = pos=(26.55,-35.2,0) rot=(0,0,1;1.5708rad)
  Radius = 0.3
FEATURE [Part::Part2DObjectPython] Line447  # Draft 2D object (typed FeaturePython)
  ChamferSize = 0
  Closed = false
  End = (39.95,-21.5,0)
  FilletRadius = 0
  Length = 13.4
  MakeFace = true
  Placement = pos=(23.75,-19,0) rot=(0,0,1;0rad)
  Points = (2) [(2.8,-2.5,0),(16.2,-2.5,0)]
  Start = (26.55,-21.5,0)
  Subdivisions = 0
FEATURE [Part::Part2DObjectPython] Arc233  # Draft 2D object (typed FeaturePython)
  FirstAngle = 90
  LastAngle = 180
  MakeFace = true
  Placement = pos=(45.55,-21.8,0) rot=(0,0,1;0rad)
  Radius = 0.3
FEATURE [Part::Part2DObjectPython] Arc234  # Draft 2D object (typed FeaturePython)
  FirstAngle = 90
  LastAngle = 180
  MakeFace = true
  Placement = pos=(96.95,-35.2,0) rot=(0,0,1;3.14159rad)
  Radius = 0.3
FEATURE [Part::Part2DObjectPython] Arc235  # Draft 2D object (typed FeaturePython)
  FirstAngle = 90
  LastAngle = 180
  MakeFace = true
  Placement = pos=(39.95,-21.8,0) rot=(0,0,-1;1.5708rad)
  Radius = 0.3
FEATURE [Part::Part2DObjectPython] Arc236  # Draft 2D object (typed FeaturePython)
  FirstAngle = 90
  LastAngle = 180
  MakeFace = true
  Placement = pos=(223.675,-21.8,0) rot=(0,0,1;0rad)
  Radius = 0.3
FEATURE [Part::Part2DObjectPython] Arc237  # Draft 2D object (typed FeaturePython)
  FirstAngle = 90
  LastAngle = 180
  MakeFace = true
  Placement = pos=(210.95,-21.8,0) rot=(0,0,-1;1.5708rad)
  Radius = 0.3
FEATURE [Part::Part2DObjectPython] Line453  # Draft 2D object (typed FeaturePython)
  ChamferSize = 0
  Closed = false
  End = (237.375,-35.2,0)
  FilletRadius = 0
  Length = 13.4
  MakeFace = true
  Placement = pos=(220.875,-19,0) rot=(0,0,1;0rad)
  Points = (2) [(16.5,-2.8,0),(16.5,-16.2,0)]
  Start = (237.375,-21.8,0)
  Subdivisions = 0
FEATURE [Part::Part2DObjectPython] Arc238  # Draft 2D object (typed FeaturePython)
  FirstAngle = 90
  LastAngle = 180
  MakeFace = true
  Placement = pos=(223.675,-35.2,0) rot=(0,0,1;1.5708rad)
  Radius = 0.3
FEATURE [Part::Part2DObjectPython] Line454  # Draft 2D object (typed FeaturePython)
  ChamferSize = 0
  Closed = false
  End = (223.375,-21.8,0)
  FilletRadius = 0
  Length = 13.4
  MakeFace = true
  Placement = pos=(220.875,-19,0) rot=(0,0,1;0rad)
  Points = (2) [(2.5,-16.2,0),(2.5,-2.8,0)]
  Start = (223.375,-35.2,0)
  Subdivisions = 0
FEATURE [Part::Part2DObjectPython] Line468  # Draft 2D object (typed FeaturePython)
  ChamferSize = 0
  Closed = false
  End = (223.675,-35.5,0)
  FilletRadius = 0
  Length = 13.4
  MakeFace = true
  Placement = pos=(220.875,-19,0) rot=(0,0,1;0rad)
  Points = (2) [(16.2,-16.5,0),(2.8,-16.5,0)]
  Start = (237.075,-35.5,0)
  Subdivisions = 0
FEATURE [Part::Part2DObjectPython] Arc243  # Draft 2D object (typed FeaturePython)
  FirstAngle = 90
  LastAngle = 180
  MakeFace = true
  Placement = pos=(237.075,-35.2,0) rot=(0,0,1;3.14159rad)
  Radius = 0.3
FEATURE [Part::Part2DObjectPython] Line469  # Draft 2D object (typed FeaturePython)
  ChamferSize = 0
  Closed = false
  End = (237.075,-21.5,0)
  FilletRadius = 0
  Length = 13.4
  MakeFace = true
  Placement = pos=(220.875,-19,0) rot=(0,0,1;0rad)
  Points = (2) [(2.8,-2.5,0),(16.2,-2.5,0)]
  Start = (223.675,-21.5,0)
  Subdivisions = 0
FEATURE [Part::Part2DObjectPython] Arc244  # Draft 2D object (typed FeaturePython)
  FirstAngle = 90
  LastAngle = 180
  MakeFace = true
  Placement = pos=(237.075,-21.8,0) rot=(0,0,-1;1.5708rad)
  Radius = 0.3
FEATURE [App::DocumentObjectGroup] Group021
  Group = -> [Arc233,Arc225,Arc221,Arc222,Line424,Line418,Line442,Line422]
FEATURE [App::DocumentObjectGroup] Group024
  Group = -> [Arc228,Arc235,Arc231,Arc232,Line447,Line444,Line443,Line446]
FEATURE [App::DocumentObjectGroup] Group026
  Group = -> [Arc223,Arc220,Arc227,Arc226,Line428,Line426,Line429,Line427]
FEATURE [App::DocumentObjectGroup] Group028
  Group = -> [Arc236,Arc244,Arc243,Arc238,Line469,Line453,Line468,Line454]
FEATURE [Part::Part2DObjectPython] Arc245  # Draft 2D object (typed FeaturePython)
  FirstAngle = 90
  LastAngle = 180
  MakeFace = true
  Placement = pos=(159.55,-35.2,0) rot=(0,0,1;1.5708rad)
  Radius = 0.3
FEATURE [Part::Part2DObjectPython] Line471  # Draft 2D object (typed FeaturePython)
  ChamferSize = 0
  Closed = false
  End = (173.25,-35.2,0)
  FilletRadius = 0
  Length = 13.4
  MakeFace = true
  Placement = pos=(156.75,-19,0) rot=(0,0,1;0rad)
  Points = (2) [(16.5,-2.8,0),(16.5,-16.2,0)]
  Start = (173.25,-21.8,0)
  Subdivisions = 0
FEATURE [Part::Part2DObjectPython] Arc246  # Draft 2D object (typed FeaturePython)
  FirstAngle = 90
  LastAngle = 180
  MakeFace = true
  Placement = pos=(153.95,-21.8,0) rot=(0,0,-1;1.5708rad)
  Radius = 0.3
FEATURE [Part::Part2DObjectPython] Arc247  # Draft 2D object (typed FeaturePython)
  FirstAngle = 90
  LastAngle = 180
  MakeFace = true
  Placement = pos=(178.55,-21.8,0) rot=(0,0,1;0rad)
  Radius = 0.3
FEATURE [Part::Part2DObjectPython] Line475  # Draft 2D object (typed FeaturePython)
  ChamferSize = 0
  Closed = false
  End = (159.55,-35.5,0)
  FilletRadius = 0
  Length = 13.4
  MakeFace = true
  Placement = pos=(156.75,-19,0) rot=(0,0,1;0rad)
  Points = (2) [(16.2,-16.5,0),(2.8,-16.5,0)]
  Start = (172.95,-35.5,0)
  Subdivisions = 0
FEATURE [Part::Part2DObjectPython] Arc248  # Draft 2D object (typed FeaturePython)
  FirstAngle = 90
  LastAngle = 180
  MakeFace = true
  Placement = pos=(172.95,-35.2,0) rot=(0,0,1;3.14159rad)
  Radius = 0.3
FEATURE [Part::Part2DObjectPython] Line477  # Draft 2D object (typed FeaturePython)
  ChamferSize = 0
  Closed = false
  End = (159.25,-21.8,0)
  FilletRadius = 0
  Length = 13.4
  MakeFace = true
  Placement = pos=(156.75,-19,0) rot=(0,0,1;0rad)
  Points = (2) [(2.5,-16.2,0),(2.5,-2.8,0)]
  Start = (159.25,-35.2,0)
  Subdivisions = 0
FEATURE [Part::Part2DObjectPython] Line478  # Draft 2D object (typed FeaturePython)
  ChamferSize = 0
  Closed = false
  End = (172.95,-21.5,0)
  FilletRadius = 0
  Length = 13.4
  MakeFace = true
  Placement = pos=(156.75,-19,0) rot=(0,0,1;0rad)
  Points = (2) [(2.8,-2.5,0),(16.2,-2.5,0)]
  Start = (159.55,-21.5,0)
  Subdivisions = 0
FEATURE [Part::Part2DObjectPython] Arc249  # Draft 2D object (typed FeaturePython)
  FirstAngle = 90
  LastAngle = 180
  MakeFace = true
  Placement = pos=(159.55,-21.8,0) rot=(0,0,1;0rad)
  Radius = 0.3
FEATURE [Part::Part2DObjectPython] Arc250  # Draft 2D object (typed FeaturePython)
  FirstAngle = 90
  LastAngle = 180
  MakeFace = true
  Placement = pos=(172.95,-21.8,0) rot=(0,0,-1;1.5708rad)
  Radius = 0.3
FEATURE [App::DocumentObjectGroup] Group020
  Group = -> [Arc249,Arc250,Arc248,Arc245,Line478,Line471,Line475,Line477]
FEATURE [Part::Part2DObjectPython] Line481  # Draft 2D object (typed FeaturePython)
  ChamferSize = 0
  Closed = false
  End = (211.25,-35.2,0)
  FilletRadius = 0
  Length = 13.4
  MakeFace = true
  Placement = pos=(194.75,-19,0) rot=(0,0,1;0rad)
  Points = (2) [(16.5,-2.8,0),(16.5,-16.2,0)]
  Start = (211.25,-21.8,0)
  Subdivisions = 0
FEATURE [Part::Part2DObjectPython] Line484  # Draft 2D object (typed FeaturePython)
  ChamferSize = 0
  Closed = false
  End = (178.55,-35.5,0)
  FilletRadius = 0
  Length = 13.4
  MakeFace = true
  Placement = pos=(175.75,-19,0) rot=(0,0,1;0rad)
  Points = (2) [(16.2,-16.5,0),(2.8,-16.5,0)]
  Start = (191.95,-35.5,0)
  Subdivisions = 0
FEATURE [Part::Part2DObjectPython] Arc251  # Draft 2D object (typed FeaturePython)
  FirstAngle = 90
  LastAngle = 180
  MakeFace = true
  Placement = pos=(191.95,-35.2,0) rot=(0,0,1;3.14159rad)
  Radius = 0.3
FEATURE [Part::Part2DObjectPython] Arc252  # Draft 2D object (typed FeaturePython)
  FirstAngle = 90
  LastAngle = 180
  MakeFace = true
  Placement = pos=(191.95,-21.8,0) rot=(0,0,-1;1.5708rad)
  Radius = 0.3
FEATURE [Part::Part2DObjectPython] Line486  # Draft 2D object (typed FeaturePython)
  ChamferSize = 0
  Closed = false
  End = (191.95,-21.5,0)
  FilletRadius = 0
  Length = 13.4
  MakeFace = true
  Placement = pos=(175.75,-19,0) rot=(0,0,1;0rad)
  Points = (2) [(2.8,-2.5,0),(16.2,-2.5,0)]
  Start = (178.55,-21.5,0)
  Subdivisions = 0
FEATURE [Part::Part2DObjectPython] Line489  # Draft 2D object (typed FeaturePython)
  ChamferSize = 0
  Closed = false
  End = (192.25,-35.2,0)
  FilletRadius = 0
  Length = 13.4
  MakeFace = true
  Placement = pos=(175.75,-19,0) rot=(0,0,1;0rad)
  Points = (2) [(16.5,-2.8,0),(16.5,-16.2,0)]
  Start = (192.25,-21.8,0)
  Subdivisions = 0
FEATURE [Part::Part2DObjectPython] Arc253  # Draft 2D object (typed FeaturePython)
  FirstAngle = 90
  LastAngle = 180
  MakeFace = true
  Placement = pos=(197.55,-21.8,0) rot=(0,0,1;0rad)
  Radius = 0.3
FEATURE [Part::Part2DObjectPython] Arc254  # Draft 2D object (typed FeaturePython)
  FirstAngle = 90
  LastAngle = 180
  MakeFace = true
  Placement = pos=(210.95,-35.2,0) rot=(0,0,1;3.14159rad)
  Radius = 0.3
FEATURE [Part::Part2DObjectPython] Line491  # Draft 2D object (typed FeaturePython)
  ChamferSize = 0
  Closed = false
  End = (197.25,-21.8,0)
  FilletRadius = 0
  Length = 13.4
  MakeFace = true
  Placement = pos=(194.75,-19,0) rot=(0,0,1;0rad)
  Points = (2) [(2.5,-16.2,0),(2.5,-2.8,0)]
  Start = (197.25,-35.2,0)
  Subdivisions = 0
FEATURE [Part::Part2DObjectPython] Line492  # Draft 2D object (typed FeaturePython)
  ChamferSize = 0
  Closed = false
  End = (197.55,-35.5,0)
  FilletRadius = 0
  Length = 13.4
  MakeFace = true
  Placement = pos=(194.75,-19,0) rot=(0,0,1;0rad)
  Points = (2) [(16.2,-16.5,0),(2.8,-16.5,0)]
  Start = (210.95,-35.5,0)
  Subdivisions = 0
FEATURE [App::DocumentObjectGroup] Group023
  Group = -> [Arc253,Arc237,Arc254,Arc229,Line430,Line481,Line492,Line491]
FEATURE [Part::Part2DObjectPython] Line493  # Draft 2D object (typed FeaturePython)
  ChamferSize = 0
  Closed = false
  End = (178.25,-21.8,0)
  FilletRadius = 0
  Length = 13.4
  MakeFace = true
  Placement = pos=(175.75,-19,0) rot=(0,0,1;0rad)
  Points = (2) [(2.5,-16.2,0),(2.5,-2.8,0)]
  Start = (178.25,-35.2,0)
  Subdivisions = 0
FEATURE [Part::Part2DObjectPython] Arc255  # Draft 2D object (typed FeaturePython)
  FirstAngle = 90
  LastAngle = 180
  MakeFace = true
  Placement = pos=(178.55,-35.2,0) rot=(0,0,1;1.5708rad)
  Radius = 0.3
FEATURE [App::DocumentObjectGroup] Group022
  Group = -> [Arc247,Arc252,Arc251,Arc255,Line486,Line489,Line484,Line493]
FEATURE [Part::Part2DObjectPython] Arc256  # Draft 2D object (typed FeaturePython)
  FirstAngle = 90
  LastAngle = 180
  MakeFace = true
  Placement = pos=(115.95,-35.2,0) rot=(0,0,1;3.14159rad)
  Radius = 0.3
FEATURE [Part::Part2DObjectPython] Arc257  # Draft 2D object (typed FeaturePython)
  FirstAngle = 90
  LastAngle = 180
  MakeFace = true
  Placement = pos=(102.55,-35.2,0) rot=(0,0,1;1.5708rad)
  Radius = 0.3
FEATURE [Part::Part2DObjectPython] Line498  # Draft 2D object (typed FeaturePython)
  ChamferSize = 0
  Closed = false
  End = (102.25,-21.8,0)
  FilletRadius = 0
  Length = 13.4
  MakeFace = true
  Placement = pos=(99.75,-19,0) rot=(0,0,1;0rad)
  Points = (2) [(2.5,-16.2,0),(2.5,-2.8,0)]
  Start = (102.25,-35.2,0)
  Subdivisions = 0
FEATURE [Part::Part2DObjectPython] Line499  # Draft 2D object (typed FeaturePython)
  ChamferSize = 0
  Closed = false
  End = (134.95,-21.5,0)
  FilletRadius = 0
  Length = 13.4
  MakeFace = true
  Placement = pos=(118.75,-19,0) rot=(0,0,1;0rad)
  Points = (2) [(2.8,-2.5,0),(16.2,-2.5,0)]
  Start = (121.55,-21.5,0)
  Subdivisions = 0
FEATURE [Part::Part2DObjectPython] Arc258  # Draft 2D object (typed FeaturePython)
  FirstAngle = 90
  LastAngle = 180
  MakeFace = true
  Placement = pos=(96.95,-21.8,0) rot=(0,0,-1;1.5708rad)
  Radius = 0.3
FEATURE [Part::Part2DObjectPython] Line501  # Draft 2D object (typed FeaturePython)
  ChamferSize = 0
  Closed = false
  End = (116.25,-35.2,0)
  FilletRadius = 0
  Length = 13.4
  MakeFace = true
  Placement = pos=(99.75,-19,0) rot=(0,0,1;0rad)
  Points = (2) [(16.5,-2.8,0),(16.5,-16.2,0)]
  Start = (116.25,-21.8,0)
  Subdivisions = 0
FEATURE [Part::Part2DObjectPython] Line503  # Draft 2D object (typed FeaturePython)
  ChamferSize = 0
  Closed = false
  End = (115.95,-21.5,0)
  FilletRadius = 0
  Length = 13.4
  MakeFace = true
  Placement = pos=(99.75,-19,0) rot=(0,0,1;0rad)
  Points = (2) [(2.8,-2.5,0),(16.2,-2.5,0)]
  Start = (102.55,-21.5,0)
  Subdivisions = 0
FEATURE [Part::Part2DObjectPython] Arc259  # Draft 2D object (typed FeaturePython)
  FirstAngle = 90
  LastAngle = 180
  MakeFace = true
  Placement = pos=(102.55,-21.8,0) rot=(0,0,1;0rad)
  Radius = 0.3
FEATURE [Part::Part2DObjectPython] Line507  # Draft 2D object (typed FeaturePython)
  ChamferSize = 0
  Closed = false
  End = (96.95,-21.5,0)
  FilletRadius = 0
  Length = 13.4
  MakeFace = true
  Placement = pos=(80.75,-19,0) rot=(0,0,1;0rad)
  Points = (2) [(2.8,-2.5,0),(16.2,-2.5,0)]
  Start = (83.55,-21.5,0)
  Subdivisions = 0
FEATURE [App::DocumentObjectGroup] Group017
  Group = -> [Arc230,Arc258,Arc234,Arc224,Line507,Line440,Line439,Line445]
FEATURE [Part::Part2DObjectPython] Arc260  # Draft 2D object (typed FeaturePython)
  FirstAngle = 90
  LastAngle = 180
  MakeFace = true
  Placement = pos=(115.95,-21.8,0) rot=(0,0,-1;1.5708rad)
  Radius = 0.3
FEATURE [Part::Part2DObjectPython] Line509  # Draft 2D object (typed FeaturePython)
  ChamferSize = 0
  Closed = false
  End = (102.55,-35.5,0)
  FilletRadius = 0
  Length = 13.4
  MakeFace = true
  Placement = pos=(99.75,-19,0) rot=(0,0,1;0rad)
  Points = (2) [(16.2,-16.5,0),(2.8,-16.5,0)]
  Start = (115.95,-35.5,0)
  Subdivisions = 0
FEATURE [App::DocumentObjectGroup] Group027
  Group = -> [Arc259,Arc260,Arc256,Arc257,Line503,Line501,Line509,Line498]
FEATURE [Part::Part2DObjectPython] Arc261  # Draft 2D object (typed FeaturePython)
  FirstAngle = 90
  LastAngle = 180
  MakeFace = true
  Placement = pos=(121.55,-21.8,0) rot=(0,0,1;0rad)
  Radius = 0.3
FEATURE [Part::Part2DObjectPython] Line511  # Draft 2D object (typed FeaturePython)
  ChamferSize = 0
  Closed = false
  End = (121.55,-35.5,0)
  FilletRadius = 0
  Length = 13.4
  MakeFace = true
  Placement = pos=(118.75,-19,0) rot=(0,0,1;0rad)
  Points = (2) [(16.2,-16.5,0),(2.8,-16.5,0)]
  Start = (134.95,-35.5,0)
  Subdivisions = 0
FEATURE [Part::Part2DObjectPython] Line513  # Draft 2D object (typed FeaturePython)
  ChamferSize = 0
  Closed = false
  End = (135.25,-35.2,0)
  FilletRadius = 0
  Length = 13.4
  MakeFace = true
  Placement = pos=(118.75,-19,0) rot=(0,0,1;0rad)
  Points = (2) [(16.5,-2.8,0),(16.5,-16.2,0)]
  Start = (135.25,-21.8,0)
  Subdivisions = 0
FEATURE [Part::Part2DObjectPython] Arc262  # Draft 2D object (typed FeaturePython)
  FirstAngle = 90
  LastAngle = 180
  MakeFace = true
  Placement = pos=(134.95,-35.2,0) rot=(0,0,1;3.14159rad)
  Radius = 0.3
FEATURE [Part::Part2DObjectPython] Line514  # Draft 2D object (typed FeaturePython)
  ChamferSize = 0
  Closed = false
  End = (121.25,-21.8,0)
  FilletRadius = 0
  Length = 13.4
  MakeFace = true
  Placement = pos=(118.75,-19,0) rot=(0,0,1;0rad)
  Points = (2) [(2.5,-16.2,0),(2.5,-2.8,0)]
  Start = (121.25,-35.2,0)
  Subdivisions = 0
FEATURE [Part::Part2DObjectPython] Arc263  # Draft 2D object (typed FeaturePython)
  FirstAngle = 90
  LastAngle = 180
  MakeFace = true
  Placement = pos=(121.55,-35.2,0) rot=(0,0,1;1.5708rad)
  Radius = 0.3
FEATURE [Part::Part2DObjectPython] Arc264  # Draft 2D object (typed FeaturePython)
  FirstAngle = 90
  LastAngle = 180
  MakeFace = true
  Placement = pos=(153.95,-35.2,0) rot=(0,0,1;3.14159rad)
  Radius = 0.3
FEATURE [Part::Part2DObjectPython] Line517  # Draft 2D object (typed FeaturePython)
  ChamferSize = 0
  Closed = false
  End = (140.55,-35.5,0)
  FilletRadius = 0
  Length = 13.4
  MakeFace = true
  Placement = pos=(137.75,-19,0) rot=(0,0,1;0rad)
  Points = (2) [(16.2,-16.5,0),(2.8,-16.5,0)]
  Start = (153.95,-35.5,0)
  Subdivisions = 0
FEATURE [Part::Part2DObjectPython] Line518  # Draft 2D object (typed FeaturePython)
  ChamferSize = 0
  Closed = false
  End = (140.25,-21.8,0)
  FilletRadius = 0
  Length = 13.4
  MakeFace = true
  Placement = pos=(137.75,-19,0) rot=(0,0,1;0rad)
  Points = (2) [(2.5,-16.2,0),(2.5,-2.8,0)]
  Start = (140.25,-35.2,0)
  Subdivisions = 0
FEATURE [Part::Part2DObjectPython] Arc265  # Draft 2D object (typed FeaturePython)
  FirstAngle = 90
  LastAngle = 180
  MakeFace = true
  Placement = pos=(134.95,-21.8,0) rot=(0,0,-1;1.5708rad)
  Radius = 0.3
FEATURE [App::DocumentObjectGroup] Group018
  Group = -> [Arc261,Arc265,Arc262,Arc263,Line499,Line513,Line511,Line514]
FEATURE [Part::Part2DObjectPython] Arc266  # Draft 2D object (typed FeaturePython)
  FirstAngle = 90
  LastAngle = 180
  MakeFace = true
  Placement = pos=(140.55,-21.8,0) rot=(0,0,1;0rad)
  Radius = 0.3
FEATURE [Part::Part2DObjectPython] Line522  # Draft 2D object (typed FeaturePython)
  ChamferSize = 0
  Closed = false
  End = (154.25,-35.2,0)
  FilletRadius = 0
  Length = 13.4
  MakeFace = true
  Placement = pos=(137.75,-19,0) rot=(0,0,1;0rad)
  Points = (2) [(16.5,-2.8,0),(16.5,-16.2,0)]
  Start = (154.25,-21.8,0)
  Subdivisions = 0
FEATURE [Part::Part2DObjectPython] Arc267  # Draft 2D object (typed FeaturePython)
  FirstAngle = 90
  LastAngle = 180
  MakeFace = true
  Placement = pos=(140.55,-35.2,0) rot=(0,0,1;1.5708rad)
  Radius = 0.3
FEATURE [Part::Part2DObjectPython] Line523  # Draft 2D object (typed FeaturePython)
  ChamferSize = 0
  Closed = false
  End = (153.95,-21.5,0)
  FilletRadius = 0
  Length = 13.4
  MakeFace = true
  Placement = pos=(137.75,-19,0) rot=(0,0,1;0rad)
  Points = (2) [(2.8,-2.5,0),(16.2,-2.5,0)]
  Start = (140.55,-21.5,0)
  Subdivisions = 0
FEATURE [App::DocumentObjectGroup] Group019
  Group = -> [Arc266,Arc246,Arc264,Arc267,Line523,Line522,Line517,Line518]
FEATURE [App::DocumentObjectGroup] Group015  label="Row 2"
  Group = -> [Group016,Group022,Group023,Group021,Group017,Group018,Group019,Group020,Group024,Group026,Group027,Group028]
FEATURE [Part::Part2DObjectPython] Line527  # Draft 2D object (typed FeaturePython)
  ChamferSize = 0
  Closed = false
  End = (131.05,-54.5,0)
  FilletRadius = 0
  Length = 13.4
  MakeFace = true
  Placement = pos=(147.25,-57,0) rot=(0,0,1;3.14159rad)
  Points = (2) [(2.8,-2.5,0),(16.2,-2.5,0)]
  Start = (144.45,-54.5,0)
  Subdivisions = 0
FEATURE [Part::Part2DObjectPython] Arc268  # Draft 2D object (typed FeaturePython)
  FirstAngle = 90
  LastAngle = 180
  MakeFace = true
  Placement = pos=(131.05,-54.2,0) rot=(0,0,1;1.5708rad)
  Radius = 0.3
FEATURE [Part::Part2DObjectPython] Arc269  # Draft 2D object (typed FeaturePython)
  FirstAngle = 90
  LastAngle = 180
  MakeFace = true
  Placement = pos=(144.45,-54.2,0) rot=(0,0,1;3.14159rad)
  Radius = 0.3
FEATURE [Part::Part2DObjectPython] Line531  # Draft 2D object (typed FeaturePython)
  ChamferSize = 0
  Closed = false
  End = (150.05,-54.5,0)
  FilletRadius = 0
  Length = 13.4
  MakeFace = true
  Placement = pos=(166.25,-57,0) rot=(0,0,1;3.14159rad)
  Points = (2) [(2.8,-2.5,0),(16.2,-2.5,0)]
  Start = (163.45,-54.5,0)
  Subdivisions = 0
FEATURE [Part::Part2DObjectPython] Line534  # Draft 2D object (typed FeaturePython)
  ChamferSize = 0
  Closed = false
  End = (68.75,-54.2,0)
  FilletRadius = 0
  Length = 13.4
  MakeFace = true
  Placement = pos=(71.25,-57,0) rot=(0,0,1;3.14159rad)
  Points = (2) [(2.5,-16.2,0),(2.5,-2.8,0)]
  Start = (68.75,-40.8,0)
  Subdivisions = 0
FEATURE [Part::Part2DObjectPython] Arc270  # Draft 2D object (typed FeaturePython)
  FirstAngle = 90
  LastAngle = 180
  MakeFace = true
  Placement = pos=(68.45,-40.8,0) rot=(0,0,-1;1.5708rad)
  Radius = 0.3
FEATURE [Part::Part2DObjectPython] Line536  # Draft 2D object (typed FeaturePython)
  ChamferSize = 0
  Closed = false
  End = (49.45,-40.5,0)
  FilletRadius = 0
  Length = 13.4
  MakeFace = true
  Placement = pos=(52.25,-57,0) rot=(0,0,1;3.14159rad)
  Points = (2) [(16.2,-16.5,0),(2.8,-16.5,0)]
  Start = (36.05,-40.5,0)
  Subdivisions = 0
FEATURE [Part::Part2DObjectPython] Line538  # Draft 2D object (typed FeaturePython)
  ChamferSize = 0
  Closed = false
  End = (74.05,-54.5,0)
  FilletRadius = 0
  Length = 13.4
  MakeFace = true
  Placement = pos=(90.25,-57,0) rot=(0,0,1;3.14159rad)
  Points = (2) [(2.8,-2.5,0),(16.2,-2.5,0)]
  Start = (87.45,-54.5,0)
  Subdivisions = 0
FEATURE [Part::Part2DObjectPython] Arc271  # Draft 2D object (typed FeaturePython)
  FirstAngle = 90
  LastAngle = 180
  MakeFace = true
  Placement = pos=(87.45,-54.2,0) rot=(0,0,1;3.14159rad)
  Radius = 0.3
FEATURE [Part::Part2DObjectPython] Arc272  # Draft 2D object (typed FeaturePython)
  FirstAngle = 90
  LastAngle = 180
  MakeFace = true
  Placement = pos=(55.05,-40.8,0) rot=(0,0,1;0rad)
  Radius = 0.3
FEATURE [Part::Part2DObjectPython] Arc273  # Draft 2D object (typed FeaturePython)
  FirstAngle = 90
  LastAngle = 180
  MakeFace = true
  Placement = pos=(74.05,-54.2,0) rot=(0,0,1;1.5708rad)
  Radius = 0.3
FEATURE [Part::Part2DObjectPython] Line542  # Draft 2D object (typed FeaturePython)
  ChamferSize = 0
  Closed = false
  End = (87.75,-54.2,0)
  FilletRadius = 0
  Length = 13.4
  MakeFace = true
  Placement = pos=(90.25,-57,0) rot=(0,0,1;3.14159rad)
  Points = (2) [(2.5,-16.2,0),(2.5,-2.8,0)]
  Start = (87.75,-40.8,0)
  Subdivisions = 0
FEATURE [Part::Part2DObjectPython] Line543  # Draft 2D object (typed FeaturePython)
  ChamferSize = 0
  Closed = false
  End = (35.75,-40.8,0)
  FilletRadius = 0
  Length = 13.4
  MakeFace = true
  Placement = pos=(52.25,-57,0) rot=(0,0,1;3.14159rad)
  Points = (2) [(16.5,-2.8,0),(16.5,-16.2,0)]
  Start = (35.75,-54.2,0)
  Subdivisions = 0
FEATURE [Part::Part2DObjectPython] Arc274  # Draft 2D object (typed FeaturePython)
  FirstAngle = 90
  LastAngle = 180
  MakeFace = true
  Placement = pos=(55.05,-54.2,0) rot=(0,0,1;1.5708rad)
  Radius = 0.3
FEATURE [Part::Part2DObjectPython] Line547  # Draft 2D object (typed FeaturePython)
  ChamferSize = 0
  Closed = false
  End = (68.45,-40.5,0)
  FilletRadius = 0
  Length = 13.4
  MakeFace = true
  Placement = pos=(71.25,-57,0) rot=(0,0,1;3.14159rad)
  Points = (2) [(16.2,-16.5,0),(2.8,-16.5,0)]
  Start = (55.05,-40.5,0)
  Subdivisions = 0
FEATURE [Part::Part2DObjectPython] Arc275  # Draft 2D object (typed FeaturePython)
  FirstAngle = 90
  LastAngle = 180
  MakeFace = true
  Placement = pos=(150.05,-54.2,0) rot=(0,0,1;1.5708rad)
  Radius = 0.3
FEATURE [Part::Part2DObjectPython] Line549  # Draft 2D object (typed FeaturePython)
  ChamferSize = 0
  Closed = false
  End = (130.75,-40.8,0)
  FilletRadius = 0
  Length = 13.4
  MakeFace = true
  Placement = pos=(147.25,-57,0) rot=(0,0,1;3.14159rad)
  Points = (2) [(16.5,-2.8,0),(16.5,-16.2,0)]
  Start = (130.75,-54.2,0)
  Subdivisions = 0
FEATURE [Part::Part2DObjectPython] Line551  # Draft 2D object (typed FeaturePython)
  ChamferSize = 0
  Closed = false
  End = (54.75,-40.8,0)
  FilletRadius = 0
  Length = 13.4
  MakeFace = true
  Placement = pos=(71.25,-57,0) rot=(0,0,1;3.14159rad)
  Points = (2) [(16.5,-2.8,0),(16.5,-16.2,0)]
  Start = (54.75,-54.2,0)
  Subdivisions = 0
FEATURE [Part::Part2DObjectPython] Line552  # Draft 2D object (typed FeaturePython)
  ChamferSize = 0
  Closed = false
  End = (55.05,-54.5,0)
  FilletRadius = 0
  Length = 13.4
  MakeFace = true
  Placement = pos=(71.25,-57,0) rot=(0,0,1;3.14159rad)
  Points = (2) [(2.8,-2.5,0),(16.2,-2.5,0)]
  Start = (68.45,-54.5,0)
  Subdivisions = 0
FEATURE [Part::Part2DObjectPython] Arc276  # Draft 2D object (typed FeaturePython)
  FirstAngle = 90
  LastAngle = 180
  MakeFace = true
  Placement = pos=(36.05,-40.8,0) rot=(0,0,1;0rad)
  Radius = 0.3
FEATURE [Part::Part2DObjectPython] Line555  # Draft 2D object (typed FeaturePython)
  ChamferSize = 0
  Closed = false
  End = (49.75,-54.2,0)
  FilletRadius = 0
  Length = 13.4
  MakeFace = true
  Placement = pos=(52.25,-57,0) rot=(0,0,1;3.14159rad)
  Points = (2) [(2.5,-16.2,0),(2.5,-2.8,0)]
  Start = (49.75,-40.8,0)
  Subdivisions = 0
FEATURE [Part::Part2DObjectPython] Arc277  # Draft 2D object (typed FeaturePython)
  FirstAngle = 90
  LastAngle = 180
  MakeFace = true
  Placement = pos=(49.45,-54.2,0) rot=(0,0,1;3.14159rad)
  Radius = 0.3
FEATURE [Part::Part2DObjectPython] Arc278  # Draft 2D object (typed FeaturePython)
  FirstAngle = 90
  LastAngle = 180
  MakeFace = true
  Placement = pos=(131.05,-40.8,0) rot=(0,0,1;0rad)
  Radius = 0.3
FEATURE [Part::Part2DObjectPython] Line558  # Draft 2D object (typed FeaturePython)
  ChamferSize = 0
  Closed = false
  End = (144.75,-54.2,0)
  FilletRadius = 0
  Length = 13.4
  MakeFace = true
  Placement = pos=(147.25,-57,0) rot=(0,0,1;3.14159rad)
  Points = (2) [(2.5,-16.2,0),(2.5,-2.8,0)]
  Start = (144.75,-40.8,0)
  Subdivisions = 0
FEATURE [Part::Part2DObjectPython] Arc279  # Draft 2D object (typed FeaturePython)
  FirstAngle = 90
  LastAngle = 180
  MakeFace = true
  Placement = pos=(144.45,-40.8,0) rot=(0,0,-1;1.5708rad)
  Radius = 0.3
FEATURE [Part::Part2DObjectPython] Line559  # Draft 2D object (typed FeaturePython)
  ChamferSize = 0
  Closed = false
  End = (112.05,-54.5,0)
  FilletRadius = 0
  Length = 13.4
  MakeFace = true
  Placement = pos=(128.25,-57,0) rot=(0,0,1;3.14159rad)
  Points = (2) [(2.8,-2.5,0),(16.2,-2.5,0)]
  Start = (125.45,-54.5,0)
  Subdivisions = 0
FEATURE [Part::Part2DObjectPython] Arc280  # Draft 2D object (typed FeaturePython)
  FirstAngle = 90
  LastAngle = 180
  MakeFace = true
  Placement = pos=(49.45,-40.8,0) rot=(0,0,-1;1.5708rad)
  Radius = 0.3
FEATURE [Part::Part2DObjectPython] Arc281  # Draft 2D object (typed FeaturePython)
  FirstAngle = 90
  LastAngle = 180
  MakeFace = true
  Placement = pos=(207.05,-54.2,0) rot=(0,0,1;1.5708rad)
  Radius = 0.3
FEATURE [Part::Part2DObjectPython] Line563  # Draft 2D object (typed FeaturePython)
  ChamferSize = 0
  Closed = false
  End = (149.75,-40.8,0)
  FilletRadius = 0
  Length = 13.4
  MakeFace = true
  Placement = pos=(166.25,-57,0) rot=(0,0,1;3.14159rad)
  Points = (2) [(16.5,-2.8,0),(16.5,-16.2,0)]
  Start = (149.75,-54.2,0)
  Subdivisions = 0
FEATURE [Part::Part2DObjectPython] Line565  # Draft 2D object (typed FeaturePython)
  ChamferSize = 0
  Closed = false
  End = (163.75,-54.2,0)
  FilletRadius = 0
  Length = 13.4
  MakeFace = true
  Placement = pos=(166.25,-57,0) rot=(0,0,1;3.14159rad)
  Points = (2) [(2.5,-16.2,0),(2.5,-2.8,0)]
  Start = (163.75,-40.8,0)
  Subdivisions = 0
FEATURE [Part::Part2DObjectPython] Arc284  # Draft 2D object (typed FeaturePython)
  FirstAngle = 90
  LastAngle = 180
  MakeFace = true
  Placement = pos=(163.45,-54.2,0) rot=(0,0,1;3.14159rad)
  Radius = 0.3
FEATURE [Part::Part2DObjectPython] Line570  # Draft 2D object (typed FeaturePython)
  ChamferSize = 0
  Closed = false
  End = (206.75,-40.8,0)
  FilletRadius = 0
  Length = 13.4
  MakeFace = true
  Placement = pos=(223.25,-57,0) rot=(0,0,1;3.14159rad)
  Points = (2) [(16.5,-2.8,0),(16.5,-16.2,0)]
  Start = (206.75,-54.2,0)
  Subdivisions = 0
FEATURE [Part::Part2DObjectPython] Arc285  # Draft 2D object (typed FeaturePython)
  FirstAngle = 90
  LastAngle = 180
  MakeFace = true
  Placement = pos=(207.05,-40.8,0) rot=(0,0,1;0rad)
  Radius = 0.3
FEATURE [Part::Part2DObjectPython] Line574  # Draft 2D object (typed FeaturePython)
  ChamferSize = 0
  Closed = false
  End = (201.45,-40.5,0)
  FilletRadius = 0
  Length = 13.4
  MakeFace = true
  Placement = pos=(204.25,-57,0) rot=(0,0,1;3.14159rad)
  Points = (2) [(16.2,-16.5,0),(2.8,-16.5,0)]
  Start = (188.05,-40.5,0)
  Subdivisions = 0
FEATURE [Part::Part2DObjectPython] Line575  # Draft 2D object (typed FeaturePython)
  ChamferSize = 0
  Closed = false
  End = (163.45,-40.5,0)
  FilletRadius = 0
  Length = 13.4
  MakeFace = true
  Placement = pos=(166.25,-57,0) rot=(0,0,1;3.14159rad)
  Points = (2) [(16.2,-16.5,0),(2.8,-16.5,0)]
  Start = (150.05,-40.5,0)
  Subdivisions = 0
FEATURE [Part::Part2DObjectPython] Arc286  # Draft 2D object (typed FeaturePython)
  FirstAngle = 90
  LastAngle = 180
  MakeFace = true
  Placement = pos=(201.45,-54.2,0) rot=(0,0,1;3.14159rad)
  Radius = 0.3
FEATURE [Part::Part2DObjectPython] Arc287  # Draft 2D object (typed FeaturePython)
  FirstAngle = 90
  LastAngle = 180
  MakeFace = true
  Placement = pos=(150.05,-40.8,0) rot=(0,0,1;0rad)
  Radius = 0.3
FEATURE [Part::Part2DObjectPython] Arc288  # Draft 2D object (typed FeaturePython)
  FirstAngle = 90
  LastAngle = 180
  MakeFace = true
  Placement = pos=(23.325,-54.2,0) rot=(0,0,1;3.14159rad)
  Radius = 0.3
FEATURE [Part::Part2DObjectPython] Arc289  # Draft 2D object (typed FeaturePython)
  FirstAngle = 90
  LastAngle = 180
  MakeFace = true
  Placement = pos=(36.05,-54.2,0) rot=(0,0,1;1.5708rad)
  Radius = 0.3
FEATURE [Part::Part2DObjectPython] Line580  # Draft 2D object (typed FeaturePython)
  ChamferSize = 0
  Closed = false
  End = (9.625,-40.8,0)
  FilletRadius = 0
  Length = 13.4
  MakeFace = true
  Placement = pos=(26.125,-57,0) rot=(0,0,1;3.14159rad)
  Points = (2) [(16.5,-2.8,0),(16.5,-16.2,0)]
  Start = (9.625,-54.2,0)
  Subdivisions = 0
FEATURE [Part::Part2DObjectPython] Arc290  # Draft 2D object (typed FeaturePython)
  FirstAngle = 90
  LastAngle = 180
  MakeFace = true
  Placement = pos=(23.325,-40.8,0) rot=(0,0,-1;1.5708rad)
  Radius = 0.3
FEATURE [Part::Part2DObjectPython] Line581  # Draft 2D object (typed FeaturePython)
  ChamferSize = 0
  Closed = false
  End = (23.625,-54.2,0)
  FilletRadius = 0
  Length = 13.4
  MakeFace = true
  Placement = pos=(26.125,-57,0) rot=(0,0,1;3.14159rad)
  Points = (2) [(2.5,-16.2,0),(2.5,-2.8,0)]
  Start = (23.625,-40.8,0)
  Subdivisions = 0
FEATURE [Part::Part2DObjectPython] Line582  # Draft 2D object (typed FeaturePython)
  ChamferSize = 0
  Closed = false
  End = (23.325,-40.5,0)
  FilletRadius = 0
  Length = 13.4
  MakeFace = true
  Placement = pos=(26.125,-57,0) rot=(0,0,1;3.14159rad)
  Points = (2) [(16.2,-16.5,0),(2.8,-16.5,0)]
  Start = (9.925,-40.5,0)
  Subdivisions = 0
FEATURE [Part::Part2DObjectPython] Arc291  # Draft 2D object (typed FeaturePython)
  FirstAngle = 90
  LastAngle = 180
  MakeFace = true
  Placement = pos=(9.925,-54.2,0) rot=(0,0,1;1.5708rad)
  Radius = 0.3
FEATURE [Part::Part2DObjectPython] Line584  # Draft 2D object (typed FeaturePython)
  ChamferSize = 0
  Closed = false
  End = (73.75,-40.8,0)
  FilletRadius = 0
  Length = 13.4
  MakeFace = true
  Placement = pos=(90.25,-57,0) rot=(0,0,1;3.14159rad)
  Points = (2) [(16.5,-2.8,0),(16.5,-16.2,0)]
  Start = (73.75,-54.2,0)
  Subdivisions = 0
FEATURE [Part::Part2DObjectPython] Arc292  # Draft 2D object (typed FeaturePython)
  FirstAngle = 90
  LastAngle = 180
  MakeFace = true
  Placement = pos=(9.925,-40.8,0) rot=(0,0,1;0rad)
  Radius = 0.3
FEATURE [Part::Part2DObjectPython] Arc293  # Draft 2D object (typed FeaturePython)
  FirstAngle = 90
  LastAngle = 180
  MakeFace = true
  Placement = pos=(93.05,-54.2,0) rot=(0,0,1;1.5708rad)
  Radius = 0.3
FEATURE [Part::Part2DObjectPython] Arc294  # Draft 2D object (typed FeaturePython)
  FirstAngle = 90
  LastAngle = 180
  MakeFace = true
  Placement = pos=(87.45,-40.8,0) rot=(0,0,-1;1.5708rad)
  Radius = 0.3
FEATURE [Part::Part2DObjectPython] Line587  # Draft 2D object (typed FeaturePython)
  ChamferSize = 0
  Closed = false
  End = (9.925,-54.5,0)
  FilletRadius = 0
  Length = 13.4
  MakeFace = true
  Placement = pos=(26.125,-57,0) rot=(0,0,1;3.14159rad)
  Points = (2) [(2.8,-2.5,0),(16.2,-2.5,0)]
  Start = (23.325,-54.5,0)
  Subdivisions = 0
FEATURE [App::DocumentObjectGroup] Group041
  Group = -> [Arc288,Arc291,Arc292,Arc290,Line587,Line580,Line582,Line581]
FEATURE [Part::Part2DObjectPython] Arc295  # Draft 2D object (typed FeaturePython)
  FirstAngle = 90
  LastAngle = 180
  MakeFace = true
  Placement = pos=(68.45,-54.2,0) rot=(0,0,1;3.14159rad)
  Radius = 0.3
FEATURE [App::DocumentObjectGroup] Group029
  Group = -> [Arc295,Arc274,Arc272,Arc270,Line552,Line551,Line547,Line534]
FEATURE [Part::Part2DObjectPython] Line589  # Draft 2D object (typed FeaturePython)
  ChamferSize = 0
  Closed = false
  End = (87.45,-40.5,0)
  FilletRadius = 0
  Length = 13.4
  MakeFace = true
  Placement = pos=(90.25,-57,0) rot=(0,0,1;3.14159rad)
  Points = (2) [(16.2,-16.5,0),(2.8,-16.5,0)]
  Start = (74.05,-40.5,0)
  Subdivisions = 0
FEATURE [Part::Part2DObjectPython] Arc296  # Draft 2D object (typed FeaturePython)
  FirstAngle = 90
  LastAngle = 180
  MakeFace = true
  Placement = pos=(74.05,-40.8,0) rot=(0,0,1;0rad)
  Radius = 0.3
FEATURE [App::DocumentObjectGroup] Group037
  Group = -> [Arc271,Arc273,Arc296,Arc294,Line538,Line584,Line589,Line542]
FEATURE [Part::Part2DObjectPython] Line591  # Draft 2D object (typed FeaturePython)
  ChamferSize = 0
  Closed = false
  End = (228.125,-40.8,0)
  FilletRadius = 0
  Length = 13.4
  MakeFace = true
  Placement = pos=(244.625,-57,0) rot=(0,0,1;3.14159rad)
  Points = (2) [(16.5,-2.8,0),(16.5,-16.2,0)]
  Start = (228.125,-54.2,0)
  Subdivisions = 0
FEATURE [Part::Part2DObjectPython] Arc298  # Draft 2D object (typed FeaturePython)
  FirstAngle = 90
  LastAngle = 180
  MakeFace = true
  Placement = pos=(228.425,-40.8,0) rot=(0,0,1;0rad)
  Radius = 0.3
FEATURE [Part::Part2DObjectPython] Arc300  # Draft 2D object (typed FeaturePython)
  FirstAngle = 90
  LastAngle = 180
  MakeFace = true
  Placement = pos=(228.425,-54.2,0) rot=(0,0,1;1.5708rad)
  Radius = 0.3
FEATURE [Part::Part2DObjectPython] Arc301  # Draft 2D object (typed FeaturePython)
  FirstAngle = 90
  LastAngle = 180
  MakeFace = true
  Placement = pos=(201.45,-40.8,0) rot=(0,0,-1;1.5708rad)
  Radius = 0.3
FEATURE [Part::Part2DObjectPython] Line596  # Draft 2D object (typed FeaturePython)
  ChamferSize = 0
  Closed = false
  End = (36.05,-54.5,0)
  FilletRadius = 0
  Length = 13.4
  MakeFace = true
  Placement = pos=(52.25,-57,0) rot=(0,0,1;3.14159rad)
  Points = (2) [(2.8,-2.5,0),(16.2,-2.5,0)]
  Start = (49.45,-54.5,0)
  Subdivisions = 0
FEATURE [App::DocumentObjectGroup] Group030
  Group = -> [Arc277,Arc289,Arc276,Arc280,Line596,Line543,Line536,Line555]
FEATURE [Part::Part2DObjectPython] Arc302  # Draft 2D object (typed FeaturePython)
  FirstAngle = 90
  LastAngle = 180
  MakeFace = true
  Placement = pos=(169.05,-54.2,0) rot=(0,0,1;1.5708rad)
  Radius = 0.3
FEATURE [Part::Part2DObjectPython] Arc303  # Draft 2D object (typed FeaturePython)
  FirstAngle = 90
  LastAngle = 180
  MakeFace = true
  Placement = pos=(188.05,-40.8,0) rot=(0,0,1;0rad)
  Radius = 0.3
FEATURE [Part::Part2DObjectPython] Arc304  # Draft 2D object (typed FeaturePython)
  FirstAngle = 90
  LastAngle = 180
  MakeFace = true
  Placement = pos=(188.05,-54.2,0) rot=(0,0,1;1.5708rad)
  Radius = 0.3
FEATURE [Part::Part2DObjectPython] Line598  # Draft 2D object (typed FeaturePython)
  ChamferSize = 0
  Closed = false
  End = (182.75,-54.2,0)
  FilletRadius = 0
  Length = 13.4
  MakeFace = true
  Placement = pos=(185.25,-57,0) rot=(0,0,1;3.14159rad)
  Points = (2) [(2.5,-16.2,0),(2.5,-2.8,0)]
  Start = (182.75,-40.8,0)
  Subdivisions = 0
FEATURE [Part::Part2DObjectPython] Line601  # Draft 2D object (typed FeaturePython)
  ChamferSize = 0
  Closed = false
  End = (182.45,-40.5,0)
  FilletRadius = 0
  Length = 13.4
  MakeFace = true
  Placement = pos=(185.25,-57,0) rot=(0,0,1;3.14159rad)
  Points = (2) [(16.2,-16.5,0),(2.8,-16.5,0)]
  Start = (169.05,-40.5,0)
  Subdivisions = 0
FEATURE [Part::Part2DObjectPython] Line603  # Draft 2D object (typed FeaturePython)
  ChamferSize = 0
  Closed = false
  End = (168.75,-40.8,0)
  FilletRadius = 0
  Length = 13.4
  MakeFace = true
  Placement = pos=(185.25,-57,0) rot=(0,0,1;3.14159rad)
  Points = (2) [(16.5,-2.8,0),(16.5,-16.2,0)]
  Start = (168.75,-54.2,0)
  Subdivisions = 0
FEATURE [Part::Part2DObjectPython] Arc305  # Draft 2D object (typed FeaturePython)
  FirstAngle = 90
  LastAngle = 180
  MakeFace = true
  Placement = pos=(182.45,-54.2,0) rot=(0,0,1;3.14159rad)
  Radius = 0.3
FEATURE [Part::Part2DObjectPython] Line605  # Draft 2D object (typed FeaturePython)
  ChamferSize = 0
  Closed = false
  End = (188.05,-54.5,0)
  FilletRadius = 0
  Length = 13.4
  MakeFace = true
  Placement = pos=(204.25,-57,0) rot=(0,0,1;3.14159rad)
  Points = (2) [(2.8,-2.5,0),(16.2,-2.5,0)]
  Start = (201.45,-54.5,0)
  Subdivisions = 0
FEATURE [Part::Part2DObjectPython] Arc306  # Draft 2D object (typed FeaturePython)
  FirstAngle = 90
  LastAngle = 180
  MakeFace = true
  Placement = pos=(163.45,-40.8,0) rot=(0,0,-1;1.5708rad)
  Radius = 0.3
FEATURE [App::DocumentObjectGroup] Group033
  Group = -> [Arc284,Arc275,Arc287,Arc306,Line531,Line563,Line575,Line565]
FEATURE [Part::Part2DObjectPython] Line606  # Draft 2D object (typed FeaturePython)
  ChamferSize = 0
  Closed = false
  End = (187.75,-40.8,0)
  FilletRadius = 0
  Length = 13.4
  MakeFace = true
  Placement = pos=(204.25,-57,0) rot=(0,0,1;3.14159rad)
  Points = (2) [(16.5,-2.8,0),(16.5,-16.2,0)]
  Start = (187.75,-54.2,0)
  Subdivisions = 0
FEATURE [Part::Part2DObjectPython] Arc307  # Draft 2D object (typed FeaturePython)
  FirstAngle = 90
  LastAngle = 180
  MakeFace = true
  Placement = pos=(182.45,-40.8,0) rot=(0,0,-1;1.5708rad)
  Radius = 0.3
FEATURE [Part::Part2DObjectPython] Line608  # Draft 2D object (typed FeaturePython)
  ChamferSize = 0
  Closed = false
  End = (169.05,-54.5,0)
  FilletRadius = 0
  Length = 13.4
  MakeFace = true
  Placement = pos=(185.25,-57,0) rot=(0,0,1;3.14159rad)
  Points = (2) [(2.8,-2.5,0),(16.2,-2.5,0)]
  Start = (182.45,-54.5,0)
  Subdivisions = 0
FEATURE [Part::Part2DObjectPython] Line609  # Draft 2D object (typed FeaturePython)
  ChamferSize = 0
  Closed = false
  End = (201.75,-54.2,0)
  FilletRadius = 0
  Length = 13.4
  MakeFace = true
  Placement = pos=(204.25,-57,0) rot=(0,0,1;3.14159rad)
  Points = (2) [(2.5,-16.2,0),(2.5,-2.8,0)]
  Start = (201.75,-40.8,0)
  Subdivisions = 0
FEATURE [App::DocumentObjectGroup] Group031
  Group = -> [Arc286,Arc304,Arc303,Arc301,Line605,Line606,Line574,Line609]
FEATURE [Part::Part2DObjectPython] Arc308  # Draft 2D object (typed FeaturePython)
  FirstAngle = 90
  LastAngle = 180
  MakeFace = true
  Placement = pos=(169.05,-40.8,0) rot=(0,0,1;0rad)
  Radius = 0.3
FEATURE [App::DocumentObjectGroup] Group039
  Group = -> [Arc305,Arc302,Arc308,Arc307,Line608,Line603,Line601,Line598]
FEATURE [Part::Part2DObjectPython] Arc309  # Draft 2D object (typed FeaturePython)
  FirstAngle = 90
  LastAngle = 180
  MakeFace = true
  Placement = pos=(125.45,-40.8,0) rot=(0,0,-1;1.5708rad)
  Radius = 0.3
FEATURE [Part::Part2DObjectPython] Arc310  # Draft 2D object (typed FeaturePython)
  FirstAngle = 90
  LastAngle = 180
  MakeFace = true
  Placement = pos=(93.05,-40.8,0) rot=(0,0,1;0rad)
  Radius = 0.3
FEATURE [Part::Part2DObjectPython] Line614  # Draft 2D object (typed FeaturePython)
  ChamferSize = 0
  Closed = false
  End = (106.45,-40.5,0)
  FilletRadius = 0
  Length = 13.4
  MakeFace = true
  Placement = pos=(109.25,-57,0) rot=(0,0,1;3.14159rad)
  Points = (2) [(16.2,-16.5,0),(2.8,-16.5,0)]
  Start = (93.05,-40.5,0)
  Subdivisions = 0
FEATURE [Part::Part2DObjectPython] Arc311  # Draft 2D object (typed FeaturePython)
  FirstAngle = 90
  LastAngle = 180
  MakeFace = true
  Placement = pos=(112.05,-54.2,0) rot=(0,0,1;1.5708rad)
  Radius = 0.3
FEATURE [Part::Part2DObjectPython] Line618  # Draft 2D object (typed FeaturePython)
  ChamferSize = 0
  Closed = false
  End = (106.75,-54.2,0)
  FilletRadius = 0
  Length = 13.4
  MakeFace = true
  Placement = pos=(109.25,-57,0) rot=(0,0,1;3.14159rad)
  Points = (2) [(2.5,-16.2,0),(2.5,-2.8,0)]
  Start = (106.75,-40.8,0)
  Subdivisions = 0
FEATURE [Part::Part2DObjectPython] Arc312  # Draft 2D object (typed FeaturePython)
  FirstAngle = 90
  LastAngle = 180
  MakeFace = true
  Placement = pos=(125.45,-54.2,0) rot=(0,0,1;3.14159rad)
  Radius = 0.3
FEATURE [Part::Part2DObjectPython] Line619  # Draft 2D object (typed FeaturePython)
  ChamferSize = 0
  Closed = false
  End = (125.45,-40.5,0)
  FilletRadius = 0
  Length = 13.4
  MakeFace = true
  Placement = pos=(128.25,-57,0) rot=(0,0,1;3.14159rad)
  Points = (2) [(16.2,-16.5,0),(2.8,-16.5,0)]
  Start = (112.05,-40.5,0)
  Subdivisions = 0
FEATURE [Part::Part2DObjectPython] Line621  # Draft 2D object (typed FeaturePython)
  ChamferSize = 0
  Closed = false
  End = (125.75,-54.2,0)
  FilletRadius = 0
  Length = 13.4
  MakeFace = true
  Placement = pos=(128.25,-57,0) rot=(0,0,1;3.14159rad)
  Points = (2) [(2.5,-16.2,0),(2.5,-2.8,0)]
  Start = (125.75,-40.8,0)
  Subdivisions = 0
FEATURE [Part::Part2DObjectPython] Line622  # Draft 2D object (typed FeaturePython)
  ChamferSize = 0
  Closed = false
  End = (92.75,-40.8,0)
  FilletRadius = 0
  Length = 13.4
  MakeFace = true
  Placement = pos=(109.25,-57,0) rot=(0,0,1;3.14159rad)
  Points = (2) [(16.5,-2.8,0),(16.5,-16.2,0)]
  Start = (92.75,-54.2,0)
  Subdivisions = 0
FEATURE [Part::Part2DObjectPython] Line624  # Draft 2D object (typed FeaturePython)
  ChamferSize = 0
  Closed = false
  End = (111.75,-40.8,0)
  FilletRadius = 0
  Length = 13.4
  MakeFace = true
  Placement = pos=(128.25,-57,0) rot=(0,0,1;3.14159rad)
  Points = (2) [(16.5,-2.8,0),(16.5,-16.2,0)]
  Start = (111.75,-54.2,0)
  Subdivisions = 0
FEATURE [Part::Part2DObjectPython] Arc313  # Draft 2D object (typed FeaturePython)
  FirstAngle = 90
  LastAngle = 180
  MakeFace = true
  Placement = pos=(112.05,-40.8,0) rot=(0,0,1;0rad)
  Radius = 0.3
FEATURE [App::DocumentObjectGroup] Group034
  Group = -> [Arc312,Arc311,Arc313,Arc309,Line559,Line624,Line619,Line621]
FEATURE [Part::Part2DObjectPython] Line625  # Draft 2D object (typed FeaturePython)
  ChamferSize = 0
  Closed = false
  End = (144.45,-40.5,0)
  FilletRadius = 0
  Length = 13.4
  MakeFace = true
  Placement = pos=(147.25,-57,0) rot=(0,0,1;3.14159rad)
  Points = (2) [(16.2,-16.5,0),(2.8,-16.5,0)]
  Start = (131.05,-40.5,0)
  Subdivisions = 0
FEATURE [App::DocumentObjectGroup] Group040
  Group = -> [Arc269,Arc268,Arc278,Arc279,Line527,Line549,Line625,Line558]
FEATURE [Part::Part2DObjectPython] Arc314  # Draft 2D object (typed FeaturePython)
  FirstAngle = 90
  LastAngle = 180
  MakeFace = true
  Placement = pos=(106.45,-54.2,0) rot=(0,0,1;3.14159rad)
  Radius = 0.3
FEATURE [Part::Part2DObjectPython] Line627  # Draft 2D object (typed FeaturePython)
  ChamferSize = 0
  Closed = false
  End = (93.05,-54.5,0)
  FilletRadius = 0
  Length = 13.4
  MakeFace = true
  Placement = pos=(109.25,-57,0) rot=(0,0,1;3.14159rad)
  Points = (2) [(2.8,-2.5,0),(16.2,-2.5,0)]
  Start = (106.45,-54.5,0)
  Subdivisions = 0
FEATURE [Part::Part2DObjectPython] Arc315  # Draft 2D object (typed FeaturePython)
  FirstAngle = 90
  LastAngle = 180
  MakeFace = true
  Placement = pos=(106.45,-40.8,0) rot=(0,0,-1;1.5708rad)
  Radius = 0.3
FEATURE [App::DocumentObjectGroup] Group036
  Group = -> [Arc314,Arc293,Arc310,Arc315,Line627,Line622,Line614,Line618]
FEATURE [Part::Part2DObjectPython] Line633  # Draft 2D object (typed FeaturePython)
  ChamferSize = 0
  Closed = false
  End = (4.875,-59.8,0)
  FilletRadius = 0
  Length = 13.4
  MakeFace = true
  Placement = pos=(21.375,-76,0) rot=(0,0,1;3.14159rad)
  Points = (2) [(16.5,-2.8,0),(16.5,-16.2,0)]
  Start = (4.875,-73.2,0)
  Subdivisions = 0
FEATURE [Part::Part2DObjectPython] Arc316  # Draft 2D object (typed FeaturePython)
  FirstAngle = 90
  LastAngle = 180
  MakeFace = true
  Placement = pos=(5.175,-73.2,0) rot=(0,0,1;1.5708rad)
  Radius = 0.3
FEATURE [Part::Part2DObjectPython] Arc317  # Draft 2D object (typed FeaturePython)
  FirstAngle = 90
  LastAngle = 180
  MakeFace = true
  Placement = pos=(5.175,-59.8,0) rot=(0,0,1;0rad)
  Radius = 0.3
FEATURE [Part::Part2DObjectPython] Line634  # Draft 2D object (typed FeaturePython)
  ChamferSize = 0
  Closed = false
  End = (5.175,-73.5,0)
  FilletRadius = 0
  Length = 13.4
  MakeFace = true
  Placement = pos=(21.375,-76,0) rot=(0,0,1;3.14159rad)
  Points = (2) [(2.8,-2.5,0),(16.2,-2.5,0)]
  Start = (18.575,-73.5,0)
  Subdivisions = 0
FEATURE [Part::Part2DObjectPython] Arc318  # Draft 2D object (typed FeaturePython)
  FirstAngle = 90
  LastAngle = 180
  MakeFace = true
  Placement = pos=(18.575,-73.2,0) rot=(0,0,1;3.14159rad)
  Radius = 0.3
FEATURE [Part::Part2DObjectPython] Line635  # Draft 2D object (typed FeaturePython)
  ChamferSize = 0
  Closed = false
  End = (18.575,-59.5,0)
  FilletRadius = 0
  Length = 13.4
  MakeFace = true
  Placement = pos=(21.375,-76,0) rot=(0,0,1;3.14159rad)
  Points = (2) [(16.2,-16.5,0),(2.8,-16.5,0)]
  Start = (5.175,-59.5,0)
  Subdivisions = 0
FEATURE [Part::Part2DObjectPython] Line636  # Draft 2D object (typed FeaturePython)
  ChamferSize = 0
  Closed = false
  End = (18.875,-73.2,0)
  FilletRadius = 0
  Length = 13.4
  MakeFace = true
  Placement = pos=(21.375,-76,0) rot=(0,0,1;3.14159rad)
  Points = (2) [(2.5,-16.2,0),(2.5,-2.8,0)]
  Start = (18.875,-59.8,0)
  Subdivisions = 0
FEATURE [Part::Part2DObjectPython] Arc319  # Draft 2D object (typed FeaturePython)
  FirstAngle = 90
  LastAngle = 180
  MakeFace = true
  Placement = pos=(18.575,-59.8,0) rot=(0,0,-1;1.5708rad)
  Radius = 0.3
FEATURE [App::DocumentObjectGroup] Group043
  Group = -> [Arc318,Arc316,Arc317,Arc319,Line634,Line633,Line635,Line636]
FEATURE [Part::Part2DObjectPython] Arc322  # Draft 2D object (typed FeaturePython)
  FirstAngle = 90
  LastAngle = 180
  MakeFace = true
  Placement = pos=(42.325,-73.2,0) rot=(0,0,1;3.14159rad)
  Radius = 0.3
FEATURE [Part::Part2DObjectPython] Line646  # Draft 2D object (typed FeaturePython)
  ChamferSize = 0
  Closed = false
  End = (42.625,-73.2,0)
  FilletRadius = 0
  Length = 13.4
  MakeFace = true
  Placement = pos=(45.125,-76,0) rot=(0,0,1;3.14159rad)
  Points = (2) [(2.5,-16.2,0),(2.5,-2.8,0)]
  Start = (42.625,-59.8,0)
  Subdivisions = 0
FEATURE [Part::Part2DObjectPython] Arc323  # Draft 2D object (typed FeaturePython)
  FirstAngle = 90
  LastAngle = 180
  MakeFace = true
  Placement = pos=(42.325,-59.8,0) rot=(0,0,-1;1.5708rad)
  Radius = 0.3
FEATURE [Part::Part2DObjectPython] Arc332  # Draft 2D object (typed FeaturePython)
  FirstAngle = 90
  LastAngle = 180
  MakeFace = true
  Placement = pos=(108.825,-73.2,0) rot=(0,0,1;3.14159rad)
  Radius = 0.3
FEATURE [Part::Part2DObjectPython] Arc334  # Draft 2D object (typed FeaturePython)
  FirstAngle = 90
  LastAngle = 180
  MakeFace = true
  Placement = pos=(108.825,-59.8,0) rot=(0,0,-1;1.5708rad)
  Radius = 0.3
FEATURE [Part::Part2DObjectPython] Arc336  # Draft 2D object (typed FeaturePython)
  FirstAngle = 90
  LastAngle = 180
  MakeFace = true
  Placement = pos=(228.425,-73.2,0) rot=(0,0,1;1.5708rad)
  Radius = 0.3
FEATURE [Part::Part2DObjectPython] Arc337  # Draft 2D object (typed FeaturePython)
  FirstAngle = 90
  LastAngle = 180
  MakeFace = true
  Placement = pos=(228.425,-59.8,0) rot=(0,0,1;0rad)
  Radius = 0.3
FEATURE [Part::Part2DObjectPython] Line677  # Draft 2D object (typed FeaturePython)
  ChamferSize = 0
  Closed = false
  End = (228.425,-73.5,0)
  FilletRadius = 0
  Length = 13.4
  MakeFace = true
  Placement = pos=(244.625,-76,0) rot=(0,0,1;3.14159rad)
  Points = (2) [(2.8,-2.5,0),(16.2,-2.5,0)]
  Start = (241.825,-73.5,0)
  Subdivisions = 0
FEATURE [Part::Part2DObjectPython] Arc338  # Draft 2D object (typed FeaturePython)
  FirstAngle = 90
  LastAngle = 180
  MakeFace = true
  Placement = pos=(241.825,-73.2,0) rot=(0,0,1;3.14159rad)
  Radius = 0.3
FEATURE [Part::Part2DObjectPython] Line678  # Draft 2D object (typed FeaturePython)
  ChamferSize = 0
  Closed = false
  End = (228.125,-59.8,0)
  FilletRadius = 0
  Length = 13.4
  MakeFace = true
  Placement = pos=(244.625,-76,0) rot=(0,0,1;3.14159rad)
  Points = (2) [(16.5,-2.8,0),(16.5,-16.2,0)]
  Start = (228.125,-73.2,0)
  Subdivisions = 0
FEATURE [Part::Part2DObjectPython] Line679  # Draft 2D object (typed FeaturePython)
  ChamferSize = 0
  Closed = false
  End = (241.825,-59.5,0)
  FilletRadius = 0
  Length = 13.4
  MakeFace = true
  Placement = pos=(244.625,-76,0) rot=(0,0,1;3.14159rad)
  Points = (2) [(16.2,-16.5,0),(2.8,-16.5,0)]
  Start = (228.425,-59.5,0)
  Subdivisions = 0
FEATURE [Part::Part2DObjectPython] Line680  # Draft 2D object (typed FeaturePython)
  ChamferSize = 0
  Closed = false
  End = (242.125,-73.2,0)
  FilletRadius = 0
  Length = 13.4
  MakeFace = true
  Placement = pos=(244.625,-76,0) rot=(0,0,1;3.14159rad)
  Points = (2) [(2.5,-16.2,0),(2.5,-2.8,0)]
  Start = (242.125,-59.8,0)
  Subdivisions = 0
FEATURE [Part::Part2DObjectPython] Arc339  # Draft 2D object (typed FeaturePython)
  FirstAngle = 90
  LastAngle = 180
  MakeFace = true
  Placement = pos=(241.825,-59.8,0) rot=(0,0,-1;1.5708rad)
  Radius = 0.3
FEATURE [App::DocumentObjectGroup] Group048
  Group = -> [Arc338,Arc336,Arc337,Arc339,Line677,Line678,Line679,Line680]
FEATURE [Part::Part2DObjectPython] Arc340  # Draft 2D object (typed FeaturePython)
  FirstAngle = 90
  LastAngle = 180
  MakeFace = true
  Placement = pos=(204.675,-73.2,0) rot=(0,0,1;1.5708rad)
  Radius = 0.3
FEATURE [Part::Part2DObjectPython] Arc341  # Draft 2D object (typed FeaturePython)
  FirstAngle = 90
  LastAngle = 180
  MakeFace = true
  Placement = pos=(204.675,-59.8,0) rot=(0,0,1;0rad)
  Radius = 0.3
FEATURE [Part::Part2DObjectPython] Line687  # Draft 2D object (typed FeaturePython)
  ChamferSize = 0
  Closed = false
  End = (204.375,-59.8,0)
  FilletRadius = 0
  Length = 13.4
  MakeFace = true
  Placement = pos=(220.875,-76,0) rot=(0,0,1;3.14159rad)
  Points = (2) [(16.5,-2.8,0),(16.5,-16.2,0)]
  Start = (204.375,-73.2,0)
  Subdivisions = 0
FEATURE [Part::Part2DObjectPython] Line709  # Draft 2D object (typed FeaturePython)
  ChamferSize = 0
  Closed = false
  End = (159.25,-59.8,0)
  FilletRadius = 0
  Length = 13.4
  MakeFace = true
  Placement = pos=(175.75,-76,0) rot=(0,0,1;3.14159rad)
  Points = (2) [(16.5,-2.8,0),(16.5,-16.2,0)]
  Start = (159.25,-73.2,0)
  Subdivisions = 0
FEATURE [Part::Part2DObjectPython] Arc350  # Draft 2D object (typed FeaturePython)
  FirstAngle = 90
  LastAngle = 180
  MakeFace = true
  Placement = pos=(159.55,-73.2,0) rot=(0,0,1;1.5708rad)
  Radius = 0.3
FEATURE [Part::Part2DObjectPython] Arc351  # Draft 2D object (typed FeaturePython)
  FirstAngle = 90
  LastAngle = 180
  MakeFace = true
  Placement = pos=(159.55,-59.8,0) rot=(0,0,1;0rad)
  Radius = 0.3
FEATURE [App::DocumentObjectGroup] Group053
FEATURE [App::DocumentObjectGroup] Group054
FEATURE [Part::Part2DObjectPython] Line746  # Draft 2D object (typed FeaturePython)
  ChamferSize = 0
  Closed = false
  End = (244.2,-2.5,0)
  FilletRadius = 0
  Length = 32.4
  MakeFace = true
  Placement = pos=(0,-76,0) rot=(0,0,1;0rad)
  Points = (2) [(211.8,73.5,0),(244.2,73.5,0)]
  Start = (211.8,-2.5,0)
  Subdivisions = 0
FEATURE [Part::Part2DObjectPython] Line752  # Draft 2D object (typed FeaturePython)
  ChamferSize = 0
  Closed = false
  End = (212.6,-16.5,0)
  FilletRadius = 0
  Length = 0.8
  MakeFace = true
  Placement = pos=(0,-76,0) rot=(0,0,1;0rad)
  Points = (2) [(211.8,59.5,0),(212.6,59.5,0)]
  Start = (211.8,-16.5,0)
  Subdivisions = 0
FEATURE [Part::Part2DObjectPython] Line753  # Draft 2D object (typed FeaturePython)
  ChamferSize = 0
  Closed = false
  End = (236.4,-16.5,0)
  FilletRadius = 0
  Length = 16.8
  MakeFace = true
  Placement = pos=(0,-76,0) rot=(0,0,1;0rad)
  Points = (2) [(219.6,59.5,0),(236.4,59.5,0)]
  Start = (219.6,-16.5,0)
  Subdivisions = 0
FEATURE [Part::Part2DObjectPython] Line754  # Draft 2D object (typed FeaturePython)
  ChamferSize = 0
  Closed = false
  End = (244.2,-16.5,0)
  FilletRadius = 0
  Length = 0.8
  MakeFace = true
  Placement = pos=(0,-76,0) rot=(0,0,1;0rad)
  Points = (2) [(243.4,59.5,0),(244.2,59.5,0)]
  Start = (243.4,-16.5,0)
  Subdivisions = 0
FEATURE [Part::Part2DObjectPython] Arc378  # Draft 2D object (typed FeaturePython)
  FirstAngle = 90
  LastAngle = 180
  MakeFace = true
  Placement = pos=(26.55,-73.2,0) rot=(0,0,1;1.5708rad)
  Radius = 0.3
FEATURE [Part::Part2DObjectPython] Arc379  # Draft 2D object (typed FeaturePython)
  FirstAngle = 90
  LastAngle = 180
  MakeFace = true
  Placement = pos=(26.55,-59.8,0) rot=(0,0,1;0rad)
  Radius = 0.3
FEATURE [Part::Part2DObjectPython] Line799  # Draft 2D object (typed FeaturePython)
  ChamferSize = 0
  Closed = false
  End = (45.25,-59.8,0)
  FilletRadius = 0
  Length = 13.4
  MakeFace = true
  Placement = pos=(61.75,-76,0) rot=(0,0,1;3.14159rad)
  Points = (2) [(16.5,-2.8,0),(16.5,-16.2,0)]
  Start = (45.25,-73.2,0)
  Subdivisions = 0
FEATURE [Part::Part2DObjectPython] Arc398  # Draft 2D object (typed FeaturePython)
  FirstAngle = 90
  LastAngle = 180
  MakeFace = true
  Placement = pos=(45.55,-73.2,0) rot=(0,0,1;1.5708rad)
  Radius = 0.3
FEATURE [Part::Part2DObjectPython] Arc399  # Draft 2D object (typed FeaturePython)
  FirstAngle = 90
  LastAngle = 180
  MakeFace = true
  Placement = pos=(45.55,-59.8,0) rot=(0,0,1;0rad)
  Radius = 0.3
FEATURE [Part::Part2DObjectPython] Arc402  # Draft 2D object (typed FeaturePython)
  FirstAngle = 90
  LastAngle = 180
  MakeFace = true
  Placement = pos=(114.425,-73.2,0) rot=(0,0,1;1.5708rad)
  Radius = 0.3
FEATURE [Part::Part2DObjectPython] Arc403  # Draft 2D object (typed FeaturePython)
  FirstAngle = 90
  LastAngle = 180
  MakeFace = true
  Placement = pos=(114.425,-59.8,0) rot=(0,0,1;0rad)
  Radius = 0.3
FEATURE [Part::Part2DObjectPython] Arc410  # Draft 2D object (typed FeaturePython)
  FirstAngle = 90
  LastAngle = 180
  MakeFace = true
  Placement = pos=(67.925,-73.2,0) rot=(0,0,1;1.5708rad)
  Radius = 0.3
FEATURE [Part::Part2DObjectPython] Line846  # Draft 2D object (typed FeaturePython)
  ChamferSize = 0
  Closed = false
  End = (167.625,-59.5,0)
  FilletRadius = 0
  Length = 8.075
  MakeFace = true
  Placement = pos=(0,-76,0) rot=(0,0,1;0rad)
  Points = (2) [(159.55,16.5,0),(167.625,16.5,0)]
  Start = (159.55,-59.5,0)
  Subdivisions = 0
FEATURE [Part::Part2DObjectPython] Line851  # Draft 2D object (typed FeaturePython)
  ChamferSize = 0
  Closed = false
  End = (114.425,-59.5,0)
  FilletRadius = 0
  Length = 7.925
  MakeFace = true
  Placement = pos=(0,-76,0) rot=(0,0,1;0rad)
  Points = (2) [(122.35,16.5,0),(114.425,16.5,0)]
  Start = (122.35,-59.5,0)
  Subdivisions = 0
FEATURE [Part::Part2DObjectPython] Line858  # Draft 2D object (typed FeaturePython)
  ChamferSize = 0
  Closed = false
  End = (42.325,-59.5,0)
  FilletRadius = 0
  Length = 15.775
  MakeFace = true
  Placement = pos=(0,-76,0) rot=(0,0,1;0rad)
  Points = (2) [(26.55,16.5,0),(42.325,16.5,0)]
  Start = (26.55,-59.5,0)
  Subdivisions = 0
FEATURE [Part::Part2DObjectPython] Line859  # Draft 2D object (typed FeaturePython)
  ChamferSize = 0
  Closed = false
  End = (42.325,-73.5,0)
  FilletRadius = 0
  Length = 15.775
  MakeFace = true
  Placement = pos=(0,-76,0) rot=(0,0,1;0rad)
  Points = (2) [(26.55,2.5,0),(42.325,2.5,0)]
  Start = (26.55,-73.5,0)
  Subdivisions = 0
FEATURE [App::DocumentObjectGroup] Group044
  Group = -> [Arc322,Arc323,Line646,Arc378,Arc379,Line858,Line859]
FEATURE [Part::Part2DObjectPython] Arc415  # Draft 2D object (typed FeaturePython)
  FirstAngle = -90
  LastAngle = 90
  MakeFace = true
  Placement = pos=(3.5,-38,0) rot=(0,0,1;0rad)
  Radius = 2.25
FEATURE [Part::Part2DObjectPython] Arc416  # Draft 2D object (typed FeaturePython)
  FirstAngle = 180
  LastAngle = 270
  MakeFace = true
  Placement = pos=(1,-35.25,0) rot=(0,0,1;0rad)
  Radius = 0.5
FEATURE [Part::Part2DObjectPython] Line868  # Draft 2D object (typed FeaturePython)
  ChamferSize = 0
  Closed = false
  End = (3.5,-35.75,0)
  FilletRadius = 0
  Length = 2.5
  MakeFace = true
  Placement = pos=(0.5,-76,0) rot=(0,0,1;0rad)
  Points = (2) [(0.5,40.25,0),(3,40.25,0)]
  Start = (1,-35.75,0)
  Subdivisions = 0
FEATURE [Part::Part2DObjectPython] Arc417  # Draft 2D object (typed FeaturePython)
  FirstAngle = 180
  LastAngle = 270
  MakeFace = true
  Placement = pos=(1,-40.75,0) rot=(0,0,-1;1.5708rad)
  Radius = 0.5
FEATURE [Part::Part2DObjectPython] Line869  # Draft 2D object (typed FeaturePython)
  ChamferSize = 0
  Closed = false
  End = (1,-40.25,0)
  FilletRadius = 0
  Length = 2.5
  MakeFace = true
  Placement = pos=(0.5,-76,0) rot=(0,0,1;0rad)
  Points = (2) [(3,35.75,0),(0.5,35.75,0)]
  Start = (3.5,-40.25,0)
  Subdivisions = 0
FEATURE [App::DocumentObjectGroup] Group058
  Group = -> [Arc415,Arc416,Line868,Arc417,Line869]
FEATURE [Part::Part2DObjectPython] Arc418  # Draft 2D object (typed FeaturePython)
  FirstAngle = -90
  LastAngle = 90
  MakeFace = true
  Placement = pos=(243.5,-38,0) rot=(0,0,1;3.14159rad)
  Radius = 2.25
FEATURE [Part::Part2DObjectPython] Line870  # Draft 2D object (typed FeaturePython)
  ChamferSize = 0
  Closed = false
  End = (243.5,-40.25,0)
  FilletRadius = 0
  Length = 2.5
  MakeFace = true
  Placement = pos=(246.5,0,0) rot=(0,0,1;3.14159rad)
  Points = (2) [(0.5,40.25,0),(3,40.25,0)]
  Start = (246,-40.25,0)
  Subdivisions = 0
FEATURE [Part::Part2DObjectPython] Line871  # Draft 2D object (typed FeaturePython)
  ChamferSize = 0
  Closed = false
  End = (246,-35.75,0)
  FilletRadius = 0
  Length = 2.5
  MakeFace = true
  Placement = pos=(246.5,0,0) rot=(0,0,1;3.14159rad)
  Points = (2) [(3,35.75,0),(0.5,35.75,0)]
  Start = (243.5,-35.75,0)
  Subdivisions = 0
FEATURE [Part::Part2DObjectPython] Arc419  # Draft 2D object (typed FeaturePython)
  FirstAngle = 180
  LastAngle = 270
  MakeFace = true
  Placement = pos=(246,-35.25,0) rot=(0,0,1;1.5708rad)
  Radius = 0.5
FEATURE [Part::Part2DObjectPython] Arc420  # Draft 2D object (typed FeaturePython)
  FirstAngle = 180
  LastAngle = 270
  MakeFace = true
  Placement = pos=(246,-40.75,0) rot=(0,0,1;3.14159rad)
  Radius = 0.5
FEATURE [App::DocumentObjectGroup] Group059
  Group = -> [Arc418,Arc420,Line870,Arc419,Line871]
FEATURE [Part::Part2DObjectPython] Arc421  # Draft 2D object (typed FeaturePython)
  FirstAngle = -180
  LastAngle = -90
  MakeFace = true
  Placement = pos=(40.2,-12.05,0) rot=(0,0,1;3.14159rad)
  Radius = 0.3
FEATURE [Part::Part2DObjectPython] Arc422  # Draft 2D object (typed FeaturePython)
  FirstAngle = -180
  LastAngle = -90
  MakeFace = true
  Placement = pos=(35.8,-6.95,0) rot=(0,0,1;0rad)
  Radius = 0.3
FEATURE [Part::Part2DObjectPython] Arc423  # Draft 2D object (typed FeaturePython)
  FirstAngle = -180
  LastAngle = -90
  MakeFace = true
  Placement = pos=(40.2,-6.95,0) rot=(0,0,1;1.5708rad)
  Radius = 0.3
FEATURE [Part::Part2DObjectPython] Arc424  # Draft 2D object (typed FeaturePython)
  FirstAngle = -180
  LastAngle = -90
  MakeFace = true
  Placement = pos=(35.8,-12.05,0) rot=(0,0,-1;1.5708rad)
  Radius = 0.3
FEATURE [Part::Part2DObjectPython] Line872  # Draft 2D object (typed FeaturePython)
  ChamferSize = 0
  Closed = false
  End = (40.2,-7.25,0)
  FilletRadius = 0
  Length = 4.4
  MakeFace = true
  Placement = pos=(0,-76,0) rot=(0,0,1;0rad)
  Points = (2) [(35.8,68.75,0),(40.2,68.75,0)]
  Start = (35.8,-7.25,0)
  Subdivisions = 0
FEATURE [Part::Part2DObjectPython] Line873  # Draft 2D object (typed FeaturePython)
  ChamferSize = 0
  Closed = false
  End = (40.2,-11.75,0)
  FilletRadius = 0
  Length = 4.4
  MakeFace = true
  Placement = pos=(0,-76,0) rot=(0,0,1;0rad)
  Points = (2) [(35.8,64.25,0),(40.2,64.25,0)]
  Start = (35.8,-11.75,0)
  Subdivisions = 0
FEATURE [Part::Part2DObjectPython] Line874  # Draft 2D object (typed FeaturePython)
  ChamferSize = 0
  Closed = false
  End = (35.5,-6.95,0)
  FilletRadius = 0
  Length = 4.15
  MakeFace = true
  Placement = pos=(0,-76,0) rot=(0,0,1;0rad)
  Points = (2) [(35.5,73.2,0),(35.5,69.05,0)]
  Start = (35.5,-2.8,0)
  Subdivisions = 0
FEATURE [Part::Part2DObjectPython] Line875  # Draft 2D object (typed FeaturePython)
  ChamferSize = 0
  Closed = false
  End = (40.5,-6.95,0)
  FilletRadius = 0
  Length = 4.15
  MakeFace = true
  Placement = pos=(0,-76,0) rot=(0,0,1;0rad)
  Points = (2) [(40.5,73.2,0),(40.5,69.05,0)]
  Start = (40.5,-2.8,0)
  Subdivisions = 0
FEATURE [Part::Part2DObjectPython] Line876  # Draft 2D object (typed FeaturePython)
  ChamferSize = 0
  Closed = false
  End = (35.5,-16.2,0)
  FilletRadius = 0
  Length = 4.15
  MakeFace = true
  Placement = pos=(0,-76,0) rot=(0,0,1;0rad)
  Points = (2) [(35.5,63.95,0),(35.5,59.8,0)]
  Start = (35.5,-12.05,0)
  Subdivisions = 0
FEATURE [Part::Part2DObjectPython] Line877  # Draft 2D object (typed FeaturePython)
  ChamferSize = 0
  Closed = false
  End = (40.5,-12.05,0)
  FilletRadius = 0
  Length = 4.15
  MakeFace = true
  Placement = pos=(0,-76,0) rot=(0,0,1;0rad)
  Points = (2) [(40.5,59.8,0),(40.5,63.95,0)]
  Start = (40.5,-16.2,0)
  Subdivisions = 0
FEATURE [App::DocumentObjectGroup] Group060
  Group = -> [Arc421,Arc422,Arc423,Arc424,Line872,Line873,Line874,Line875,Line876,Line877]
FEATURE [Part::Part2DObjectPython] Line884  # Draft 2D object (typed FeaturePython)
  ChamferSize = 0
  Closed = false
  End = (206.5,-6.95,0)
  FilletRadius = 0
  Length = 4.15
  MakeFace = true
  Placement = pos=(171,-76,0) rot=(0,0,1;0rad)
  Points = (2) [(35.5,73.2,0),(35.5,69.05,0)]
  Start = (206.5,-2.8,0)
  Subdivisions = 0
FEATURE [Part::Part2DObjectPython] Line885  # Draft 2D object (typed FeaturePython)
  ChamferSize = 0
  Closed = false
  End = (211.5,-6.95,0)
  FilletRadius = 0
  Length = 4.15
  MakeFace = true
  Placement = pos=(171,-76,0) rot=(0,0,1;0rad)
  Points = (2) [(40.5,73.2,0),(40.5,69.05,0)]
  Start = (211.5,-2.8,0)
  Subdivisions = 0
FEATURE [Part::Part2DObjectPython] Line886  # Draft 2D object (typed FeaturePython)
  ChamferSize = 0
  Closed = false
  End = (206.5,-16.2,0)
  FilletRadius = 0
  Length = 4.15
  MakeFace = true
  Placement = pos=(171,-76,0) rot=(0,0,1;0rad)
  Points = (2) [(35.5,63.95,0),(35.5,59.8,0)]
  Start = (206.5,-12.05,0)
  Subdivisions = 0
FEATURE [Part::Part2DObjectPython] Arc429  # Draft 2D object (typed FeaturePython)
  FirstAngle = -180
  LastAngle = -90
  MakeFace = true
  Placement = pos=(206.8,-6.95,0) rot=(0,0,1;0rad)
  Radius = 0.3
FEATURE [Part::Part2DObjectPython] Arc430  # Draft 2D object (typed FeaturePython)
  FirstAngle = -180
  LastAngle = -90
  MakeFace = true
  Placement = pos=(211.2,-12.05,0) rot=(0,0,1;3.14159rad)
  Radius = 0.3
FEATURE [Part::Part2DObjectPython] Arc431  # Draft 2D object (typed FeaturePython)
  FirstAngle = -180
  LastAngle = -90
  MakeFace = true
  Placement = pos=(206.8,-12.05,0) rot=(0,0,-1;1.5708rad)
  Radius = 0.3
FEATURE [Part::Part2DObjectPython] Line887  # Draft 2D object (typed FeaturePython)
  ChamferSize = 0
  Closed = false
  End = (211.2,-11.75,0)
  FilletRadius = 0
  Length = 4.4
  MakeFace = true
  Placement = pos=(171,-76,0) rot=(0,0,1;0rad)
  Points = (2) [(35.8,64.25,0),(40.2,64.25,0)]
  Start = (206.8,-11.75,0)
  Subdivisions = 0
FEATURE [Part::Part2DObjectPython] Arc432  # Draft 2D object (typed FeaturePython)
  FirstAngle = -180
  LastAngle = -90
  MakeFace = true
  Placement = pos=(211.2,-6.95,0) rot=(0,0,1;1.5708rad)
  Radius = 0.3
FEATURE [Part::Part2DObjectPython] Line888  # Draft 2D object (typed FeaturePython)
  ChamferSize = 0
  Closed = false
  End = (211.5,-12.05,0)
  FilletRadius = 0
  Length = 4.15
  MakeFace = true
  Placement = pos=(171,-76,0) rot=(0,0,1;0rad)
  Points = (2) [(40.5,59.8,0),(40.5,63.95,0)]
  Start = (211.5,-16.2,0)
  Subdivisions = 0
FEATURE [Part::Part2DObjectPython] Line889  # Draft 2D object (typed FeaturePython)
  ChamferSize = 0
  Closed = false
  End = (211.2,-7.25,0)
  FilletRadius = 0
  Length = 4.4
  MakeFace = true
  Placement = pos=(171,-76,0) rot=(0,0,1;0rad)
  Points = (2) [(35.8,68.75,0),(40.2,68.75,0)]
  Start = (206.8,-7.25,0)
  Subdivisions = 0
FEATURE [App::DocumentObjectGroup] Group062
  Group = -> [Arc430,Arc429,Arc432,Arc431,Line889,Line887,Line884,Line885,Line886,Line888]
FEATURE [Part::Part2DObjectPython] Line892  # Draft 2D object (typed FeaturePython)
  ChamferSize = 0
  Closed = false
  End = (109.125,-63.95,0)
  FilletRadius = 0
  Length = 4.15
  MakeFace = true
  Placement = pos=(73.625,-133,0) rot=(0,0,1;0rad)
  Points = (2) [(35.5,73.2,0),(35.5,69.05,0)]
  Start = (109.125,-59.8,0)
  Subdivisions = 0
FEATURE [Part::Part2DObjectPython] Line893  # Draft 2D object (typed FeaturePython)
  ChamferSize = 0
  Closed = false
  End = (113.825,-68.75,0)
  FilletRadius = 0
  Length = 4.4
  MakeFace = true
  Placement = pos=(73.625,-133,0) rot=(0,0,1;0rad)
  Points = (2) [(35.8,64.25,0),(40.2,64.25,0)]
  Start = (109.425,-68.75,0)
  Subdivisions = 0
FEATURE [Part::Part2DObjectPython] Arc433  # Draft 2D object (typed FeaturePython)
  FirstAngle = -180
  LastAngle = -90
  MakeFace = true
  Placement = pos=(109.425,-69.05,0) rot=(0,0,-1;1.5708rad)
  Radius = 0.3
FEATURE [Part::Part2DObjectPython] Arc434  # Draft 2D object (typed FeaturePython)
  FirstAngle = -180
  LastAngle = -90
  MakeFace = true
  Placement = pos=(113.825,-63.95,0) rot=(0,0,1;1.5708rad)
  Radius = 0.3
FEATURE [Part::Part2DObjectPython] Line894  # Draft 2D object (typed FeaturePython)
  ChamferSize = 0
  Closed = false
  End = (114.125,-63.95,0)
  FilletRadius = 0
  Length = 4.15
  MakeFace = true
  Placement = pos=(73.625,-133,0) rot=(0,0,1;0rad)
  Points = (2) [(40.5,73.2,0),(40.5,69.05,0)]
  Start = (114.125,-59.8,0)
  Subdivisions = 0
FEATURE [Part::Part2DObjectPython] Arc435  # Draft 2D object (typed FeaturePython)
  FirstAngle = -180
  LastAngle = -90
  MakeFace = true
  Placement = pos=(109.425,-63.95,0) rot=(0,0,1;0rad)
  Radius = 0.3
FEATURE [Part::Part2DObjectPython] Line895  # Draft 2D object (typed FeaturePython)
  ChamferSize = 0
  Closed = false
  End = (109.125,-73.2,0)
  FilletRadius = 0
  Length = 4.15
  MakeFace = true
  Placement = pos=(73.625,-133,0) rot=(0,0,1;0rad)
  Points = (2) [(35.5,63.95,0),(35.5,59.8,0)]
  Start = (109.125,-69.05,0)
  Subdivisions = 0
FEATURE [Part::Part2DObjectPython] Arc436  # Draft 2D object (typed FeaturePython)
  FirstAngle = -180
  LastAngle = -90
  MakeFace = true
  Placement = pos=(113.825,-69.05,0) rot=(0,0,1;3.14159rad)
  Radius = 0.3
FEATURE [Part::Part2DObjectPython] Line896  # Draft 2D object (typed FeaturePython)
  ChamferSize = 0
  Closed = false
  End = (114.125,-69.05,0)
  FilletRadius = 0
  Length = 4.15
  MakeFace = true
  Placement = pos=(73.625,-133,0) rot=(0,0,1;0rad)
  Points = (2) [(40.5,59.8,0),(40.5,63.95,0)]
  Start = (114.125,-73.2,0)
  Subdivisions = 0
FEATURE [Part::Part2DObjectPython] Line897  # Draft 2D object (typed FeaturePython)
  ChamferSize = 0
  Closed = false
  End = (113.825,-64.25,0)
  FilletRadius = 0
  Length = 4.4
  MakeFace = true
  Placement = pos=(73.625,-133,0) rot=(0,0,1;0rad)
  Points = (2) [(35.8,68.75,0),(40.2,68.75,0)]
  Start = (109.425,-64.25,0)
  Subdivisions = 0
FEATURE [App::DocumentObjectGroup] Group063
  Group = -> [Arc436,Arc435,Arc434,Arc433,Line897,Line893,Line892,Line894,Line895,Line896]
FEATURE [Part::Part2DObjectPython] Arc437  # Draft 2D object (typed FeaturePython)
  FirstAngle = -90
  LastAngle = 90
  MakeFace = true
  Placement = pos=(23.5,-66.5,0) rot=(0,0,1;3.14159rad)
  Radius = 2.25
FEATURE [Part::Part2DObjectPython] Arc438  # Draft 2D object (typed FeaturePython)
  FirstAngle = 180
  LastAngle = 270
  MakeFace = true
  Placement = pos=(25.75,-63.75,0) rot=(0,0,1;1.5708rad)
  Radius = 0.5
FEATURE [Part::Part2DObjectPython] Arc439  # Draft 2D object (typed FeaturePython)
  FirstAngle = 180
  LastAngle = 270
  MakeFace = true
  Placement = pos=(25.75,-69.25,0) rot=(0,0,1;3.14159rad)
  Radius = 0.5
FEATURE [Part::Part2DObjectPython] Line898  # Draft 2D object (typed FeaturePython)
  ChamferSize = 0
  Closed = false
  End = (26.25,-63.75,0)
  FilletRadius = 0
  Length = 3.95
  MakeFace = true
  Placement = pos=(0,-76,0) rot=(0,0,1;0rad)
  Points = (2) [(26.25,16.2,0),(26.25,12.25,0)]
  Start = (26.25,-59.8,0)
  Subdivisions = 0
FEATURE [Part::Part2DObjectPython] Line899  # Draft 2D object (typed FeaturePython)
  ChamferSize = 0
  Closed = false
  End = (25.75,-64.25,0)
  FilletRadius = 0
  Length = 2.25
  MakeFace = true
  Placement = pos=(0,-76,0) rot=(0,0,1;0rad)
  Points = (2) [(23.5,11.75,0),(25.75,11.75,0)]
  Start = (23.5,-64.25,0)
  Subdivisions = 0
FEATURE [Part::Part2DObjectPython] Line900  # Draft 2D object (typed FeaturePython)
  ChamferSize = 0
  Closed = false
  End = (25.75,-68.75,0)
  FilletRadius = 0
  Length = 2.25
  MakeFace = true
  Placement = pos=(0,-76,0) rot=(0,0,1;0rad)
  Points = (2) [(23.5,7.25,0),(25.75,7.25,0)]
  Start = (23.5,-68.75,0)
  Subdivisions = 0
FEATURE [Part::Part2DObjectPython] Line901  # Draft 2D object (typed FeaturePython)
  ChamferSize = 0
  Closed = false
  End = (26.25,-73.2,0)
  FilletRadius = 0
  Length = 3.95
  MakeFace = true
  Placement = pos=(0,-76,0) rot=(0,0,1;0rad)
  Points = (2) [(26.25,6.75,0),(26.25,2.8,0)]
  Start = (26.25,-69.25,0)
  Subdivisions = 0
FEATURE [App::DocumentObjectGroup] Group064
  Group = -> [Arc437,Arc439,Arc438,Line898,Line899,Line900,Line901]
FEATURE [Part::Part2DObjectPython] Line906  # Draft 2D object (typed FeaturePython)
  ChamferSize = 0
  Closed = false
  End = (111.5,-6.95,0)
  FilletRadius = 0
  Length = 4.15
  MakeFace = true
  Placement = pos=(76,-76,0) rot=(0,0,1;0rad)
  Points = (2) [(35.5,73.2,0),(35.5,69.05,0)]
  Start = (111.5,-2.8,0)
  Subdivisions = 0
FEATURE [Part::Part2DObjectPython] Arc440  # Draft 2D object (typed FeaturePython)
  FirstAngle = -180
  LastAngle = -90
  MakeFace = true
  Placement = pos=(111.8,-12.05,0) rot=(0,0,-1;1.5708rad)
  Radius = 0.3
FEATURE [Part::Part2DObjectPython] Arc441  # Draft 2D object (typed FeaturePython)
  FirstAngle = -180
  LastAngle = -90
  MakeFace = true
  Placement = pos=(116.2,-12.05,0) rot=(0,0,1;3.14159rad)
  Radius = 0.3
FEATURE [Part::Part2DObjectPython] Arc442  # Draft 2D object (typed FeaturePython)
  FirstAngle = -180
  LastAngle = -90
  MakeFace = true
  Placement = pos=(111.8,-6.95,0) rot=(0,0,1;0rad)
  Radius = 0.3
FEATURE [Part::Part2DObjectPython] Arc443  # Draft 2D object (typed FeaturePython)
  FirstAngle = -180
  LastAngle = -90
  MakeFace = true
  Placement = pos=(116.2,-6.95,0) rot=(0,0,1;1.5708rad)
  Radius = 0.3
FEATURE [Part::Part2DObjectPython] Line907  # Draft 2D object (typed FeaturePython)
  ChamferSize = 0
  Closed = false
  End = (116.2,-7.25,0)
  FilletRadius = 0
  Length = 4.4
  MakeFace = true
  Placement = pos=(76,-76,0) rot=(0,0,1;0rad)
  Points = (2) [(35.8,68.75,0),(40.2,68.75,0)]
  Start = (111.8,-7.25,0)
  Subdivisions = 0
FEATURE [Part::Part2DObjectPython] Line908  # Draft 2D object (typed FeaturePython)
  ChamferSize = 0
  Closed = false
  End = (116.2,-11.75,0)
  FilletRadius = 0
  Length = 4.4
  MakeFace = true
  Placement = pos=(76,-76,0) rot=(0,0,1;0rad)
  Points = (2) [(35.8,64.25,0),(40.2,64.25,0)]
  Start = (111.8,-11.75,0)
  Subdivisions = 0
FEATURE [Part::Part2DObjectPython] Line909  # Draft 2D object (typed FeaturePython)
  ChamferSize = 0
  Closed = false
  End = (116.5,-6.95,0)
  FilletRadius = 0
  Length = 4.15
  MakeFace = true
  Placement = pos=(76,-76,0) rot=(0,0,1;0rad)
  Points = (2) [(40.5,73.2,0),(40.5,69.05,0)]
  Start = (116.5,-2.8,0)
  Subdivisions = 0
FEATURE [Part::Part2DObjectPython] Line910  # Draft 2D object (typed FeaturePython)
  ChamferSize = 0
  Closed = false
  End = (111.5,-16.2,0)
  FilletRadius = 0
  Length = 4.15
  MakeFace = true
  Placement = pos=(76,-76,0) rot=(0,0,1;0rad)
  Points = (2) [(35.5,63.95,0),(35.5,59.8,0)]
  Start = (111.5,-12.05,0)
  Subdivisions = 0
FEATURE [Part::Part2DObjectPython] Line911  # Draft 2D object (typed FeaturePython)
  ChamferSize = 0
  Closed = false
  End = (116.5,-12.05,0)
  FilletRadius = 0
  Length = 4.15
  MakeFace = true
  Placement = pos=(76,-76,0) rot=(0,0,1;0rad)
  Points = (2) [(40.5,59.8,0),(40.5,63.95,0)]
  Start = (116.5,-16.2,0)
  Subdivisions = 0
FEATURE [App::DocumentObjectGroup] Group068
  Group = -> [Arc441,Arc442,Arc443,Arc440,Line907,Line908,Line906,Line909,Line910,Line911]
FEATURE [Part::Part2DObjectPython] Circle  label="Reset"  # Draft 2D object (typed FeaturePython)
  FirstAngle = 0
  LastAngle = 0
  MakeFace = false
  Placement = pos=(28,-47.5,0) rot=(0,0,1;0rad)
  Radius = 2
FEATURE [Part::Part2DObjectPython] Line926  # Draft 2D object (typed FeaturePython)
  ChamferSize = 0
  Closed = false
  End = (244.5,-0.5,0)
  FilletRadius = 0
  Length = 242
  MakeFace = true
  Placement = pos=(0,-76,0) rot=(0,0,1;0rad)
  Points = (2) [(2.5,75.5,0),(244.5,75.5,0)]
  Start = (2.5,-0.5,0)
  Subdivisions = 0
FEATURE [Part::Part2DObjectPython] Line927  # Draft 2D object (typed FeaturePython)
  ChamferSize = 0
  Closed = false
  End = (246.5,-35.25,0)
  FilletRadius = 0
  Length = 32.75
  MakeFace = true
  Placement = pos=(0,-76,0) rot=(0,0,1;0rad)
  Points = (2) [(246.5,73.5,0),(246.5,40.75,0)]
  Start = (246.5,-2.5,0)
  Subdivisions = 0
FEATURE [Part::Part2DObjectPython] Line928  # Draft 2D object (typed FeaturePython)
  ChamferSize = 0
  Closed = false
  End = (246.5,-73.5,0)
  FilletRadius = 0
  Length = 32.75
  MakeFace = true
  Placement = pos=(0,-76,0) rot=(0,0,1;0rad)
  Points = (2) [(246.5,35.25,0),(246.5,2.5,0)]
  Start = (246.5,-40.75,0)
  Subdivisions = 0
FEATURE [Part::Part2DObjectPython] Line929  # Draft 2D object (typed FeaturePython)
  ChamferSize = 0
  Closed = false
  End = (2.5,-75.5,0)
  FilletRadius = 0
  Length = 242
  MakeFace = true
  Placement = pos=(0,-76,0) rot=(0,0,1;0rad)
  Points = (2) [(244.5,0.5,0),(2.5,0.5,0)]
  Start = (244.5,-75.5,0)
  Subdivisions = 0
FEATURE [Part::Part2DObjectPython] Line930  # Draft 2D object (typed FeaturePython)
  ChamferSize = 0
  Closed = false
  End = (0.5,-40.75,0)
  FilletRadius = 0
  Length = 32.75
  MakeFace = true
  Placement = pos=(0,-76,0) rot=(0,0,1;0rad)
  Points = (2) [(0.5,2.5,0),(0.5,35.25,0)]
  Start = (0.5,-73.5,0)
  Subdivisions = 0
FEATURE [Part::Part2DObjectPython] Line931  # Draft 2D object (typed FeaturePython)
  ChamferSize = 0
  Closed = false
  End = (0.5,-2.5,0)
  FilletRadius = 0
  Length = 32.75
  MakeFace = true
  Placement = pos=(0,-76,0) rot=(0,0,1;0rad)
  Points = (2) [(0.5,40.75,0),(0.5,73.5,0)]
  Start = (0.5,-35.25,0)
  Subdivisions = 0
FEATURE [App::DocumentObjectGroup] Group067  label="Border"
  Group = -> [Arc212,Arc213,Arc214,Arc215,Line926,Line927,Line928,Line929,Line930,Line931,Group058,Group059]
FEATURE [Part::Part2DObjectPython] Arc444  # Draft 2D object (typed FeaturePython)
  FirstAngle = 180
  LastAngle = 270
  MakeFace = true
  Placement = pos=(213.6,-17,0) rot=(0,0,1;0rad)
  Radius = 1
FEATURE [Part::Part2DObjectPython] Arc445  # Draft 2D object (typed FeaturePython)
  FirstAngle = -90
  LastAngle = 0
  MakeFace = true
  Placement = pos=(218.6,-17,0) rot=(0,0,1;0rad)
  Radius = 1
FEATURE [Part::Part2DObjectPython] Line932  # Draft 2D object (typed FeaturePython)
  ChamferSize = 0
  Closed = false
  End = (218.6,-18,0)
  FilletRadius = 0
  Length = 5
  MakeFace = true
  Placement = pos=(0,-76.5,0) rot=(0,0,1;0rad)
  Points = (2) [(213.6,58.5,0),(218.6,58.5,0)]
  Start = (213.6,-18,0)
  Subdivisions = 0
FEATURE [Part::Part2DObjectPython] Line933  # Draft 2D object (typed FeaturePython)
  ChamferSize = 0
  Closed = false
  End = (242.4,-18,0)
  FilletRadius = 0
  Length = 5
  MakeFace = true
  Placement = pos=(23.8,-76.5,0) rot=(0,0,1;0rad)
  Points = (2) [(213.6,58.5,0),(218.6,58.5,0)]
  Start = (237.4,-18,0)
  Subdivisions = 0
FEATURE [Part::Part2DObjectPython] Arc446  # Draft 2D object (typed FeaturePython)
  FirstAngle = 180
  LastAngle = 270
  MakeFace = true
  Placement = pos=(237.4,-17,0) rot=(0,0,1;0rad)
  Radius = 1
FEATURE [Part::Part2DObjectPython] Arc447  # Draft 2D object (typed FeaturePython)
  FirstAngle = -90
  LastAngle = 0
  MakeFace = true
  Placement = pos=(242.4,-17,0) rot=(0,0,1;0rad)
  Radius = 1
FEATURE [Part::Part2DObjectPython] Line934  # Draft 2D object (typed FeaturePython)
  ChamferSize = 0
  Closed = false
  End = (236.4,-17,0)
  FilletRadius = 0
  Length = 0.5
  MakeFace = true
  Placement = pos=(0,-76,0) rot=(0,0,1;0rad)
  Points = (2) [(236.4,59.5,0),(236.4,59,0)]
  Start = (236.4,-16.5,0)
  Subdivisions = 0
FEATURE [Part::Part2DObjectPython] Line935  # Draft 2D object (typed FeaturePython)
  ChamferSize = 0
  Closed = false
  End = (243.4,-16.5,0)
  FilletRadius = 0
  Length = 0.5
  MakeFace = true
  Placement = pos=(0,-76,0) rot=(0,0,1;0rad)
  Points = (2) [(243.4,59,0),(243.4,59.5,0)]
  Start = (243.4,-17,0)
  Subdivisions = 0
FEATURE [Part::Part2DObjectPython] Line936  # Draft 2D object (typed FeaturePython)
  ChamferSize = 0
  Closed = false
  End = (212.6,-16.5,0)
  FilletRadius = 0
  Length = 0.5
  MakeFace = true
  Placement = pos=(0,-76,0) rot=(0,0,1;0rad)
  Points = (2) [(212.6,59,0),(212.6,59.5,0)]
  Start = (212.6,-17,0)
  Subdivisions = 0
FEATURE [Part::Part2DObjectPython] Line937  # Draft 2D object (typed FeaturePython)
  ChamferSize = 0
  Closed = false
  End = (219.6,-16.5,0)
  FilletRadius = 0
  Length = 0.5
  MakeFace = true
  Placement = pos=(0,-76,0) rot=(0,0,1;0rad)
  Points = (2) [(219.6,59,0),(219.6,59.5,0)]
  Start = (219.6,-17,0)
  Subdivisions = 0
FEATURE [App::DocumentObjectGroup] Group069
  Group = -> [Line933,Arc446,Arc447,Line934,Line935]
FEATURE [App::DocumentObjectGroup] Group070
  Group = -> [Line936,Arc444,Line932,Arc445,Line937]
FEATURE [App::DocumentObjectGroup] Group055
  Group = -> [Line746,Line752,Line753,Line754,Group069,Group070,Line136,Arc048,Arc050,Arc055,Arc054]
FEATURE [App::DocumentObjectGroup] Group014  label="Row 1"
  Group = -> [Group,Group001,Group002,Group003,Group004,Group005,Group006,Group007,Group009,Group010,Group011,Group055]
FEATURE [Part::Part2DObjectPython] Arc448  # Draft 2D object (typed FeaturePython)
  FirstAngle = -90
  LastAngle = 0
  MakeFace = true
  Placement = pos=(187.65,-59,0) rot=(0,0,1;3.14159rad)
  Radius = 1
FEATURE [Part::Part2DObjectPython] Arc449  # Draft 2D object (typed FeaturePython)
  FirstAngle = 180
  LastAngle = 270
  MakeFace = true
  Placement = pos=(192.65,-59,0) rot=(0,0,1;3.14159rad)
  Radius = 1
FEATURE [Part::Part2DObjectPython] Line938  # Draft 2D object (typed FeaturePython)
  ChamferSize = 0
  Closed = false
  End = (193.65,-59,0)
  FilletRadius = 0
  Length = 0.5
  MakeFace = true
  Placement = pos=(430.05,-2.8e-14,0) rot=(0,0,1;3.14159rad)
  Points = (2) [(236.4,59.5,0),(236.4,59,0)]
  Start = (193.65,-59.5,0)
  Subdivisions = 0
FEATURE [Part::Part2DObjectPython] Line939  # Draft 2D object (typed FeaturePython)
  ChamferSize = 0
  Closed = false
  End = (187.65,-58,0)
  FilletRadius = 0
  Length = 5
  MakeFace = true
  Placement = pos=(406.25,0.5,0) rot=(0,0,1;3.14159rad)
  Points = (2) [(213.6,58.5,0),(218.6,58.5,0)]
  Start = (192.65,-58,0)
  Subdivisions = 0
FEATURE [Part::Part2DObjectPython] Line940  # Draft 2D object (typed FeaturePython)
  ChamferSize = 0
  Closed = false
  End = (186.65,-59.5,0)
  FilletRadius = 0
  Length = 0.5
  MakeFace = true
  Placement = pos=(430.05,-2.8e-14,0) rot=(0,0,1;3.14159rad)
  Points = (2) [(243.4,59,0),(243.4,59.5,0)]
  Start = (186.65,-59,0)
  Subdivisions = 0
FEATURE [App::DocumentObjectGroup] Group071
  Group = -> [Line939,Arc449,Arc448,Line938,Line940]
FEATURE [Part::Part2DObjectPython] Arc450  # Draft 2D object (typed FeaturePython)
  FirstAngle = -90
  LastAngle = 0
  MakeFace = true
  Placement = pos=(168.625,-59,0) rot=(0,0,1;3.14159rad)
  Radius = 1
FEATURE [Part::Part2DObjectPython] Arc451  # Draft 2D object (typed FeaturePython)
  FirstAngle = 180
  LastAngle = 270
  MakeFace = true
  Placement = pos=(173.625,-59,0) rot=(0,0,1;3.14159rad)
  Radius = 1
FEATURE [Part::Part2DObjectPython] Line942  # Draft 2D object (typed FeaturePython)
  ChamferSize = 0
  Closed = false
  End = (168.625,-58,0)
  FilletRadius = 0
  Length = 5
  MakeFace = true
  Placement = pos=(387.225,0.5,0) rot=(0,0,1;3.14159rad)
  Points = (2) [(213.6,58.5,0),(218.6,58.5,0)]
  Start = (173.625,-58,0)
  Subdivisions = 0
FEATURE [Part::Part2DObjectPython] Line943  # Draft 2D object (typed FeaturePython)
  ChamferSize = 0
  Closed = false
  End = (167.625,-59.5,0)
  FilletRadius = 0
  Length = 0.5
  MakeFace = true
  Placement = pos=(411.025,-2.8e-14,0) rot=(0,0,1;3.14159rad)
  Points = (2) [(243.4,59,0),(243.4,59.5,0)]
  Start = (167.625,-59,0)
  Subdivisions = 0
FEATURE [App::DocumentObjectGroup] Group072
  Group = -> [Line942,Arc451,Arc450,Line943]
FEATURE [Part::Part2DObjectPython] Arc452  # Draft 2D object (typed FeaturePython)
  FirstAngle = -90
  LastAngle = 0
  MakeFace = true
  Placement = pos=(123.35,-59,0) rot=(0,0,1;3.14159rad)
  Radius = 1
FEATURE [Part::Part2DObjectPython] Line947  # Draft 2D object (typed FeaturePython)
  ChamferSize = 0
  Closed = false
  End = (122.35,-59.5,0)
  FilletRadius = 0
  Length = 0.5
  MakeFace = true
  Placement = pos=(365.75,-2.8e-14,0) rot=(0,0,1;3.14159rad)
  Points = (2) [(243.4,59,0),(243.4,59.5,0)]
  Start = (122.35,-59,0)
  Subdivisions = 0
FEATURE [App::DocumentObjectGroup] Group073
  Group = -> [Arc452,Line947]
FEATURE [Part::Part2DObjectPython] Arc455  # Draft 2D object (typed FeaturePython)
  FirstAngle = -90
  LastAngle = 0
  MakeFace = true
  Placement = pos=(147.15,-59,0) rot=(0,0,1;3.14159rad)
  Radius = 1
FEATURE [Part::Part2DObjectPython] Arc457  # Draft 2D object (typed FeaturePython)
  FirstAngle = -90
  LastAngle = 0
  MakeFace = true
  Placement = pos=(68.625,-59,0) rot=(0,0,1;3.14159rad)
  Radius = 1
FEATURE [Part::Part2DObjectPython] Line956  # Draft 2D object (typed FeaturePython)
  ChamferSize = 0
  Closed = false
  End = (67.625,-73.2,0)
  FilletRadius = 0
  Length = 14.2
  MakeFace = true
  Placement = pos=(0,-76,0) rot=(0,0,1;0rad)
  Points = (2) [(67.625,17,0),(67.625,2.8,0)]
  Start = (67.625,-59,0)
  Subdivisions = 0
FEATURE [App::DocumentObjectGroup] Group075
  Group = -> [Arc457,Line956]
FEATURE [Part::Part2DObjectPython] Arc458  # Draft 2D object (typed FeaturePython)
  FirstAngle = -90
  LastAngle = 0
  MakeFace = true
  Placement = pos=(154.525,-72.5,0) rot=(0,0,1;0rad)
  Radius = 1
FEATURE [Part::Part2DObjectPython] Line959  # Draft 2D object (typed FeaturePython)
  ChamferSize = 0
  Closed = false
  End = (155.525,-59,0)
  FilletRadius = 0
  Length = 13.5
  MakeFace = true
  Placement = pos=(2.375,-76,0) rot=(0,0,1;0rad)
  Points = (2) [(153.15,3.5,0),(153.15,17,0)]
  Start = (155.525,-72.5,0)
  Subdivisions = 0
FEATURE [Part::Part2DObjectPython] Circle011  label="Caps indicator"  # Draft 2D object (typed FeaturePython)
  FirstAngle = 0
  LastAngle = 0
  MakeFace = false
  Placement = pos=(22,-28.5,0) rot=(0,0,1;0rad)
  Radius = 1.5
FEATURE [Part::Part2DObjectPython] Arc465  # Draft 2D object (typed FeaturePython)
  FirstAngle = 90
  LastAngle = 180
  MakeFace = true
  Placement = pos=(66.075,-73.2,0) rot=(0,0,1;3.14159rad)
  Radius = 0.3
FEATURE [Part::Part2DObjectPython] Line968  # Draft 2D object (typed FeaturePython)
  ChamferSize = 0
  Closed = false
  End = (66.375,-73.2,0)
  FilletRadius = 0
  Length = 13.4
  MakeFace = true
  Placement = pos=(68.875,-76,0) rot=(0,0,1;3.14159rad)
  Points = (2) [(2.5,-16.2,0),(2.5,-2.8,0)]
  Start = (66.375,-59.8,0)
  Subdivisions = 0
FEATURE [Part::Part2DObjectPython] Arc467  # Draft 2D object (typed FeaturePython)
  FirstAngle = 90
  LastAngle = 180
  MakeFace = true
  Placement = pos=(66.075,-59.8,0) rot=(0,0,-1;1.5708rad)
  Radius = 0.3
FEATURE [Part::Part2DObjectPython] Arc468  # Draft 2D object (typed FeaturePython)
  FirstAngle = 90
  LastAngle = 180
  MakeFace = true
  Placement = pos=(85.925,-73.2,0) rot=(0,0,1;1.5708rad)
  Radius = 0.3
FEATURE [Part::Part2DObjectPython] Arc470  # Draft 2D object (typed FeaturePython)
  FirstAngle = 90
  LastAngle = 180
  MakeFace = true
  Placement = pos=(85.925,-59.8,0) rot=(0,0,1;0rad)
  Radius = 0.3
FEATURE [Part::Part2DObjectPython] Line973  # Draft 2D object (typed FeaturePython)
  ChamferSize = 0
  Closed = false
  End = (85.625,-59.8,0)
  FilletRadius = 0
  Length = 13.4
  MakeFace = true
  Placement = pos=(102.125,-76,0) rot=(0,0,1;3.14159rad)
  Points = (2) [(16.5,-2.8,0),(16.5,-16.2,0)]
  Start = (85.625,-73.2,0)
  Subdivisions = 0
FEATURE [Part::Part2DObjectPython] Arc482  # Draft 2D object (typed FeaturePython)
  FirstAngle = 180
  LastAngle = 270
  MakeFace = true
  Placement = pos=(83.225,-59,0) rot=(0,0,1;3.14159rad)
  Radius = 1
FEATURE [Part::Part2DObjectPython] Arc484  # Draft 2D object (typed FeaturePython)
  FirstAngle = 180
  LastAngle = 270
  MakeFace = true
  Placement = pos=(154.525,-59,0) rot=(0,0,1;3.14159rad)
  Radius = 1
FEATURE [Part::Part2DObjectPython] Line994  # Draft 2D object (typed FeaturePython)
  ChamferSize = 0
  Closed = false
  End = (131.725,-59,0)
  FilletRadius = 0
  Length = 0.5
  MakeFace = true
  Placement = pos=(368.125,-2.8e-14,0) rot=(0,0,1;3.14159rad)
  Points = (2) [(236.4,59.5,0),(236.4,59,0)]
  Start = (131.725,-59.5,0)
  Subdivisions = 0
FEATURE [Part::Part2DObjectPython] Arc486  # Draft 2D object (typed FeaturePython)
  FirstAngle = 180
  LastAngle = 270
  MakeFace = true
  Placement = pos=(130.725,-59,0) rot=(0,0,1;3.14159rad)
  Radius = 1
FEATURE [Part::Part2DObjectPython] Line1007  # Draft 2D object (typed FeaturePython)
  ChamferSize = 0
  Closed = false
  End = (201.75,-73.2,0)
  FilletRadius = 0
  Length = 13.4
  MakeFace = true
  Placement = pos=(204.25,-76,0) rot=(0,0,1;3.14159rad)
  Points = (2) [(2.5,-16.2,0),(2.5,-2.8,0)]
  Start = (201.75,-59.8,0)
  Subdivisions = 0
FEATURE [Part::Part2DObjectPython] Arc493  # Draft 2D object (typed FeaturePython)
  FirstAngle = 90
  LastAngle = 180
  MakeFace = true
  Placement = pos=(201.45,-59.8,0) rot=(0,0,-1;1.5708rad)
  Radius = 0.3
FEATURE [Part::Part2DObjectPython] Arc494  # Draft 2D object (typed FeaturePython)
  FirstAngle = 90
  LastAngle = 180
  MakeFace = true
  Placement = pos=(201.45,-73.2,0) rot=(0,0,1;3.14159rad)
  Radius = 0.3
FEATURE [Part::Part2DObjectPython] Arc496  # Draft 2D object (typed FeaturePython)
  FirstAngle = 90
  LastAngle = 180
  MakeFace = true
  Placement = pos=(220.45,-73.2,0) rot=(0,0,1;3.14159rad)
  Radius = 0.3
FEATURE [Part::Part2DObjectPython] Arc497  # Draft 2D object (typed FeaturePython)
  FirstAngle = 90
  LastAngle = 180
  MakeFace = true
  Placement = pos=(220.45,-59.8,0) rot=(0,0,-1;1.5708rad)
  Radius = 0.3
FEATURE [Part::Part2DObjectPython] Line1013  # Draft 2D object (typed FeaturePython)
  ChamferSize = 0
  Closed = false
  End = (83.225,-58,0)
  FilletRadius = 0
  Length = 14.6
  MakeFace = true
  Placement = pos=(0,-76,0) rot=(0,0,1;0rad)
  Points = (2) [(68.625,18,0),(83.225,18,0)]
  Start = (68.625,-58,0)
  Subdivisions = 0
FEATURE [Part::Part2DObjectPython] Line1016  # Draft 2D object (typed FeaturePython)
  ChamferSize = 0
  Closed = false
  End = (66.075,-59.5,0)
  FilletRadius = 0
  Length = 20.525
  MakeFace = true
  Placement = pos=(0,-76,0) rot=(0,0,1;0rad)
  Points = (2) [(45.55,16.5,0),(66.075,16.5,0)]
  Start = (45.55,-59.5,0)
  Subdivisions = 0
FEATURE [Part::Part2DObjectPython] Line1017  # Draft 2D object (typed FeaturePython)
  ChamferSize = 0
  Closed = false
  End = (45.55,-73.5,0)
  FilletRadius = 0
  Length = 20.525
  MakeFace = true
  Placement = pos=(0,-76,0) rot=(0,0,1;0rad)
  Points = (2) [(66.075,2.5,0),(45.55,2.5,0)]
  Start = (66.075,-73.5,0)
  Subdivisions = 0
FEATURE [App::DocumentObjectGroup] Group045
  Group = -> [Arc398,Arc399,Line799,Arc465,Line968,Arc467,Line1016,Line1017]
FEATURE [Part::Part2DObjectPython] Arc500  # Draft 2D object (typed FeaturePython)
  FirstAngle = 180
  LastAngle = 270
  MakeFace = true
  Placement = pos=(83.225,-72.5,0) rot=(0,0,1;1.5708rad)
  Radius = 1
FEATURE [Part::Part2DObjectPython] Line1018  # Draft 2D object (typed FeaturePython)
  ChamferSize = 0
  Closed = false
  End = (83.225,-73.5,0)
  FilletRadius = 0
  Length = 15.3
  MakeFace = true
  Placement = pos=(0,-76,0) rot=(0,0,1;0rad)
  Points = (2) [(67.925,2.5,0),(83.225,2.5,0)]
  Start = (67.925,-73.5,0)
  Subdivisions = 0
FEATURE [Part::Part2DObjectPython] Line1019  # Draft 2D object (typed FeaturePython)
  ChamferSize = 0
  Closed = false
  End = (84.225,-59,0)
  FilletRadius = 0
  Length = 13.5
  MakeFace = true
  Placement = pos=(0,-76,0) rot=(0,0,1;0rad)
  Points = (2) [(84.225,3.5,0),(84.225,17,0)]
  Start = (84.225,-72.5,0)
  Subdivisions = 0
FEATURE [App::DocumentObjectGroup] Group046
  Group = -> [Arc410,Group075,Arc500,Line1018,Line1019,Line1013,Arc482]
FEATURE [Part::Part2DObjectPython] Line1020  # Draft 2D object (typed FeaturePython)
  ChamferSize = 0
  Closed = false
  End = (101.025,-59.5,0)
  FilletRadius = 0
  Length = 15.1
  MakeFace = true
  Placement = pos=(0,-76,0) rot=(0,0,1;0rad)
  Points = (2) [(85.925,16.5,0),(101.025,16.5,0)]
  Start = (85.925,-59.5,0)
  Subdivisions = 0
FEATURE [Part::Part2DObjectPython] Line1021  # Draft 2D object (typed FeaturePython)
  ChamferSize = 0
  Closed = false
  End = (108.825,-59.5,0)
  FilletRadius = 0
  Length = 0.8
  MakeFace = true
  Placement = pos=(0,-76,0) rot=(0,0,1;0rad)
  Points = (2) [(108.025,16.5,0),(108.825,16.5,0)]
  Start = (108.025,-59.5,0)
  Subdivisions = 0
FEATURE [Part::Part2DObjectPython] Line1022  # Draft 2D object (typed FeaturePython)
  ChamferSize = 0
  Closed = false
  End = (85.925,-73.5,0)
  FilletRadius = 0
  Length = 22.9
  MakeFace = true
  Placement = pos=(0,-76,0) rot=(0,0,1;0rad)
  Points = (2) [(108.825,2.5,0),(85.925,2.5,0)]
  Start = (108.825,-73.5,0)
  Subdivisions = 0
FEATURE [Part::Part2DObjectPython] Line1023  # Draft 2D object (typed FeaturePython)
  ChamferSize = 0
  Closed = false
  End = (101.025,-59.5,0)
  FilletRadius = 0
  Length = 0.5
  MakeFace = true
  Placement = pos=(320.625,-2.8e-14,0) rot=(0,0,1;3.14159rad)
  Points = (2) [(219.6,59,0),(219.6,59.5,0)]
  Start = (101.025,-59,0)
  Subdivisions = 0
FEATURE [Part::Part2DObjectPython] Arc501  # Draft 2D object (typed FeaturePython)
  FirstAngle = -90
  LastAngle = 0
  MakeFace = true
  Placement = pos=(102.025,-59,0) rot=(0,0,1;3.14159rad)
  Radius = 1
FEATURE [Part::Part2DObjectPython] Line1024  # Draft 2D object (typed FeaturePython)
  ChamferSize = 0
  Closed = false
  End = (102.025,-58,0)
  FilletRadius = 0
  Length = 5
  MakeFace = true
  Placement = pos=(320.625,0.5,0) rot=(0,0,1;3.14159rad)
  Points = (2) [(213.6,58.5,0),(218.6,58.5,0)]
  Start = (107.025,-58,0)
  Subdivisions = 0
FEATURE [Part::Part2DObjectPython] Arc502  # Draft 2D object (typed FeaturePython)
  FirstAngle = 180
  LastAngle = 270
  MakeFace = true
  Placement = pos=(107.025,-59,0) rot=(0,0,1;3.14159rad)
  Radius = 1
FEATURE [Part::Part2DObjectPython] Line1025  # Draft 2D object (typed FeaturePython)
  ChamferSize = 0
  Closed = false
  End = (108.025,-59.5,0)
  FilletRadius = 0
  Length = 0.5
  MakeFace = true
  Placement = pos=(320.625,-2.8e-14,0) rot=(0,0,1;3.14159rad)
  Points = (2) [(212.6,59,0),(212.6,59.5,0)]
  Start = (108.025,-59,0)
  Subdivisions = 0
FEATURE [App::DocumentObjectGroup] Group047
  Group = -> [Arc332,Arc334,Line1021,Line1020,Line1022,Arc468,Arc470,Line973,Line1023,Arc501,Line1024,Arc502,Line1025]
FEATURE [Part::Part2DObjectPython] Line1026  # Draft 2D object (typed FeaturePython)
  ChamferSize = 0
  Closed = false
  End = (220.45,-59.5,0)
  FilletRadius = 0
  Length = 15.775
  MakeFace = true
  Placement = pos=(0,-76,0) rot=(0,0,1;0rad)
  Points = (2) [(204.675,16.5,0),(220.45,16.5,0)]
  Start = (204.675,-59.5,0)
  Subdivisions = 0
FEATURE [Part::Part2DObjectPython] Line1027  # Draft 2D object (typed FeaturePython)
  ChamferSize = 0
  Closed = false
  End = (220.45,-73.5,0)
  FilletRadius = 0
  Length = 15.775
  MakeFace = true
  Placement = pos=(0,-76,0) rot=(0,0,1;0rad)
  Points = (2) [(204.675,2.5,0),(220.45,2.5,0)]
  Start = (204.675,-73.5,0)
  Subdivisions = 0
FEATURE [App::DocumentObjectGroup] Group049
  Group = -> [Arc340,Arc341,Line687,Arc497,Arc496,Line1026,Line1027]
FEATURE [Part::Part2DObjectPython] Line1028  # Draft 2D object (typed FeaturePython)
  ChamferSize = 0
  Closed = false
  End = (174.625,-59.5,0)
  FilletRadius = 0
  Length = 12.025
  MakeFace = true
  Placement = pos=(0,-76,0) rot=(0,0,1;0rad)
  Points = (2) [(186.65,16.5,0),(174.625,16.5,0)]
  Start = (186.65,-59.5,0)
  Subdivisions = 0
FEATURE [Part::Part2DObjectPython] Line1029  # Draft 2D object (typed FeaturePython)
  ChamferSize = 0
  Closed = false
  End = (174.625,-59,0)
  FilletRadius = 0
  Length = 0.5
  MakeFace = true
  Placement = pos=(0,-76,0) rot=(0,0,1;0rad)
  Points = (2) [(174.625,16.5,0),(174.625,17,0)]
  Start = (174.625,-59.5,0)
  Subdivisions = 0
FEATURE [Part::Part2DObjectPython] Line1030  # Draft 2D object (typed FeaturePython)
  ChamferSize = 0
  Closed = false
  End = (201.45,-59.5,0)
  FilletRadius = 0
  Length = 7.8
  MakeFace = true
  Placement = pos=(0,-76,0) rot=(0,0,1;0rad)
  Points = (2) [(193.65,16.5,0),(201.45,16.5,0)]
  Start = (193.65,-59.5,0)
  Subdivisions = 0
FEATURE [Part::Part2DObjectPython] Line  # Draft 2D object (typed FeaturePython)
  ChamferSize = 0
  Closed = false
  End = (201.45,-73.5,0)
  FilletRadius = 0
  Length = 41.9
  MakeFace = true
  Placement = pos=(0,-76,0) rot=(0,0,1;0rad)
  Points = (2) [(159.55,2.5,0),(201.45,2.5,0)]
  Start = (159.55,-73.5,0)
  Subdivisions = 0
FEATURE [App::DocumentObjectGroup] Group050
  Group = -> [Group071,Arc350,Arc351,Line709,Line846,Group072,Line1028,Line1029,Line1030,Line,Line1007,Arc493,Arc494]
FEATURE [Part::Part2DObjectPython] Line1033  # Draft 2D object (typed FeaturePython)
  ChamferSize = 0
  Closed = false
  End = (146.15,-59,0)
  FilletRadius = 0
  Length = 0.5
  MakeFace = true
  Placement = pos=(0,-76,0) rot=(0,0,1;0rad)
  Points = (2) [(146.15,16.5,0),(146.15,17,0)]
  Start = (146.15,-59.5,0)
  Subdivisions = 0
FEATURE [Part::Part2DObjectPython] Line1034  # Draft 2D object (typed FeaturePython)
  ChamferSize = 0
  Closed = false
  End = (146.15,-59.5,0)
  FilletRadius = 0
  Length = 14.425
  MakeFace = true
  Placement = pos=(0,-76,0) rot=(0,0,1;0rad)
  Points = (2) [(131.725,16.5,0),(146.15,16.5,0)]
  Start = (131.725,-59.5,0)
  Subdivisions = 0
FEATURE [Part::Part2DObjectPython] Line1035  # Draft 2D object (typed FeaturePython)
  ChamferSize = 0
  Closed = false
  End = (130.725,-58,0)
  FilletRadius = 0
  Length = 7.375
  MakeFace = true
  Placement = pos=(0,-76,0) rot=(0,0,1;0rad)
  Points = (2) [(123.35,18,0),(130.725,18,0)]
  Start = (123.35,-58,0)
  Subdivisions = 0
FEATURE [Part::Part2DObjectPython] Line1036  # Draft 2D object (typed FeaturePython)
  ChamferSize = 0
  Closed = false
  End = (154.525,-58,0)
  FilletRadius = 0
  Length = 7.375
  MakeFace = true
  Placement = pos=(0,-76,0) rot=(0,0,1;0rad)
  Points = (2) [(147.15,18,0),(154.525,18,0)]
  Start = (147.15,-58,0)
  Subdivisions = 0
FEATURE [Part::Part2DObjectPython] Line1037  # Draft 2D object (typed FeaturePython)
  ChamferSize = 0
  Closed = false
  End = (154.525,-73.5,0)
  FilletRadius = 0
  Length = 40.1
  MakeFace = true
  Placement = pos=(0,-76,0) rot=(0,0,1;0rad)
  Points = (2) [(114.425,2.5,0),(154.525,2.5,0)]
  Start = (114.425,-73.5,0)
  Subdivisions = 0
FEATURE [App::DocumentObjectGroup] Group052
  Group = -> [Group054,Group053,Arc402,Arc403,Line851,Group073,Arc484,Line994,Arc486,Line1033,Line1034,Line1035,Arc455,Arc458,Line959,Line1037,Line1036]
FEATURE [App::DocumentObjectGroup] Group042  label="Row 4"
  Group = -> [Group043,Group044,Group046,Group045,Group047,Group048,Group049,Group050,Group052]
FEATURE [Part::Part2DObjectPython] Arc503  # Draft 2D object (typed FeaturePython)
  FirstAngle = -90
  LastAngle = 90
  MakeFace = true
  Placement = pos=(223.25,-66.5,0) rot=(0,0,1;0rad)
  Radius = 2.25
FEATURE [Part::Part2DObjectPython] Line1038  # Draft 2D object (typed FeaturePython)
  ChamferSize = 0
  Closed = false
  End = (220.75,-64.25,0)
  FilletRadius = 0
  Length = 2.5
  MakeFace = true
  Placement = pos=(0,-76,0) rot=(0,0,1;0rad)
  Points = (2) [(223.25,11.75,0),(220.75,11.75,0)]
  Start = (223.25,-64.25,0)
  Subdivisions = 0
FEATURE [Part::Part2DObjectPython] Line1039  # Draft 2D object (typed FeaturePython)
  ChamferSize = 0
  Closed = false
  End = (220.75,-68.75,0)
  FilletRadius = 0
  Length = 2.5
  MakeFace = true
  Placement = pos=(0,-76,0) rot=(0,0,1;0rad)
  Points = (2) [(223.25,7.25,0),(220.75,7.25,0)]
  Start = (223.25,-68.75,0)
  Subdivisions = 0
FEATURE [Part::Part2DObjectPython] Line1040  # Draft 2D object (typed FeaturePython)
  ChamferSize = 0
  Closed = false
  End = (220.75,-64.25,0)
  FilletRadius = 0
  Length = 4.45
  MakeFace = true
  Placement = pos=(0,-76,0) rot=(0,0,1;0rad)
  Points = (2) [(220.75,16.2,0),(220.75,11.75,0)]
  Start = (220.75,-59.8,0)
  Subdivisions = 0
FEATURE [Part::Part2DObjectPython] Line1041  # Draft 2D object (typed FeaturePython)
  ChamferSize = 0
  Closed = false
  End = (220.75,-73.2,0)
  FilletRadius = 0
  Length = 4.45
  MakeFace = true
  Placement = pos=(0,-76,0) rot=(0,0,1;0rad)
  Points = (2) [(220.75,7.25,0),(220.75,2.8,0)]
  Start = (220.75,-68.75,0)
  Subdivisions = 0
FEATURE [App::DocumentObjectGroup] Group076
  Group = -> [Arc503,Line1038,Line1039,Line1040,Line1041]
FEATURE [App::DocumentObjectGroup] Group065  label="Holes"
  Group = -> [Group060,Group062,Group063,Group064,Group068,Group076]
FEATURE [Part::Part2DObjectPython] Arc505  # Draft 2D object (typed FeaturePython)
  FirstAngle = 90
  LastAngle = 180
  MakeFace = true
  Placement = pos=(244.2,-40.8,0) rot=(0,0,-1;1.5708rad)
  Radius = 0.3
FEATURE [Part::Part2DObjectPython] Line1046  # Draft 2D object (typed FeaturePython)
  ChamferSize = 0
  Closed = false
  End = (244.5,-54.2,0)
  FilletRadius = 0
  Length = 13.4
  MakeFace = true
  Placement = pos=(247,-57,0) rot=(0,0,1;3.14159rad)
  Points = (2) [(2.5,-16.2,0),(2.5,-2.8,0)]
  Start = (244.5,-40.8,0)
  Subdivisions = 0
FEATURE [Part::Part2DObjectPython] Arc506  # Draft 2D object (typed FeaturePython)
  FirstAngle = 90
  LastAngle = 180
  MakeFace = true
  Placement = pos=(244.2,-54.2,0) rot=(0,0,1;3.14159rad)
  Radius = 0.3
FEATURE [Part::Part2DObjectPython] Arc509  # Draft 2D object (typed FeaturePython)
  FirstAngle = 90
  LastAngle = 180
  MakeFace = true
  Placement = pos=(222.825,-40.8,0) rot=(0,0,-1;1.5708rad)
  Radius = 0.3
FEATURE [Part::Part2DObjectPython] Line1053  # Draft 2D object (typed FeaturePython)
  ChamferSize = 0
  Closed = false
  End = (223.125,-54.2,0)
  FilletRadius = 0
  Length = 13.4
  MakeFace = true
  Placement = pos=(225.625,-57,0) rot=(0,0,1;3.14159rad)
  Points = (2) [(2.5,-16.2,0),(2.5,-2.8,0)]
  Start = (223.125,-40.8,0)
  Subdivisions = 0
FEATURE [Part::Part2DObjectPython] Arc510  # Draft 2D object (typed FeaturePython)
  FirstAngle = 90
  LastAngle = 180
  MakeFace = true
  Placement = pos=(222.825,-54.2,0) rot=(0,0,1;3.14159rad)
  Radius = 0.3
FEATURE [Part::Part2DObjectPython] Line1054  # Draft 2D object (typed FeaturePython)
  ChamferSize = 0
  Closed = false
  End = (244.2,-40.5,0)
  FilletRadius = 0
  Length = 15.775
  MakeFace = true
  Placement = pos=(228.425,-40.5,0) rot=(0,0,1;0rad)
  Points = (2) [(0,0,0),(15.775,0,0)]
  Start = (228.425,-40.5,0)
  Subdivisions = 0
FEATURE [Part::Part2DObjectPython] Line1055  # Draft 2D object (typed FeaturePython)
  ChamferSize = 0
  Closed = false
  End = (228.425,-54.5,0)
  FilletRadius = 0
  Length = 15.775
  MakeFace = true
  Placement = pos=(244.2,-54.5,0) rot=(0,0,1;0rad)
  Points = (2) [(0,0,0),(-15.775,0,0)]
  Start = (244.2,-54.5,0)
  Subdivisions = 0
FEATURE [App::DocumentObjectGroup] Group035
  Group = -> [Arc300,Arc298,Line591,Line1055,Line1054,Arc505,Line1046,Arc506]
FEATURE [Part::Part2DObjectPython] Line1056  # Draft 2D object (typed FeaturePython)
  ChamferSize = 0
  Closed = false
  End = (222.825,-54.5,0)
  FilletRadius = 0
  Length = 15.775
  MakeFace = true
  Placement = pos=(207.05,-54.5,0) rot=(0,0,1;0rad)
  Points = (2) [(0,0,0),(15.775,-7.10543e-15,0)]
  Start = (207.05,-54.5,0)
  Subdivisions = 0
FEATURE [Part::Part2DObjectPython] Line1057  # Draft 2D object (typed FeaturePython)
  ChamferSize = 0
  Closed = false
  End = (207.05,-40.5,0)
  FilletRadius = 0
  Length = 15.775
  MakeFace = true
  Placement = pos=(222.825,-40.5,0) rot=(0,0,1;0rad)
  Points = (2) [(0,0,0),(-15.775,0,0)]
  Start = (222.825,-40.5,0)
  Subdivisions = 0
FEATURE [App::DocumentObjectGroup] Group038
  Group = -> [Arc281,Arc285,Line570,Line1057,Line1056,Arc510,Line1053,Arc509]
FEATURE [App::DocumentObjectGroup] Group032  label="Row 3"
  Group = -> [Group035,Group029,Group030,Group031,Group033,Group034,Group036,Group037,Group038,Group039,Group040,Group041]
FEATURE [App::DocumentObjectGroup] Group066  label="Switches"
  Group = -> [Group014,Group015,Group032,Group042]
